# Revit family: ESTW
name_source: partatom
category: Mechanical Equipment
revit_build: Autodesk Revit 2018 (Build: 20170223_1515(x64)
units: mm (PartAtom-declared; Revit-internal decimal feet)

## family parameters
Always vertical = Yes
Cut with Voids When Loaded = No
Part Type = Normal
Room Calculation Point = No
Round Connector Dimension = Use Radius
Shared = No
Work Plane-Based = No

## types (192) — shared parameters
Description = Series Fan Powered Air Terminal with ECM Motor and Hot Water Coil
Discharge Flange = 1"
Discharge Height "Y" = 17 1/2"
Enclosure Depth = 6 1/2"
Enclosure Length = 22 1/4"
Enclosure Width = 11 1/8"
HWC Conn "B" = 3 3/8"
HWC Conn "C" = 1 39/64"
HWC Conn Top = 1 7/16"
HWConnec Length = 4"
Inlet S dim = 5 1/2"
Manufacturer = Anemostat
Model = ESTW
URL = http://www.anemostat.com

## per-type parameters (varying)
- ESTW 1/2-hp - 06L 1ROW COIL W/O S/ELBOW: Connector Bottom LH=Yes; Connector Bottom RH=No; Connector Top LH=Yes; Connector Top RH=No; Diameter=5 7/8"; Discharge Width "X"=20"; Duct Inlet Radius=3"; Elbow for LH=No; Elbow for RH=No; Enclosure for LH=Yes; Enclosure for RH=No; HWC Conn=0"; HWC Depth "Z"=12 1/4"; HWC for LH=Yes; HWC for RH=No; Height=18"; Induction Width "C"=17"; Induction for LH=Yes; Induction for RH=No; Inlet for LH=Yes; Inlet for RH=No; Length=40"; Q5A=18"; Q5B=20"; Q5Q=18"; Radius=2 15/16"; Width=40"
- ESTW 1-hp - 09L 1ROW COIL W/O S/ELBOW: Connector Bottom LH=Yes; Connector Bottom RH=No; Connector Top LH=Yes; Connector Top RH=No; Diameter=8 7/8"; Discharge Width "X"=24"; Duct Inlet Radius=4"; Elbow for LH=No; Elbow for RH=No; Enclosure for LH=Yes; Enclosure for RH=No; HWC Conn=0"; HWC Depth "Z"=12 1/4"; HWC for LH=Yes; HWC for RH=No; Height=20"; Induction Width "C"=21"; Induction for LH=Yes; Induction for RH=No; Inlet for LH=Yes; Inlet for RH=No; Length=48"; Q5A=20"; Q5B=24"; Q5Q=20"; Radius=4 7/16"; Width=48"
- ESTW 1/3-hp - 08L 1ROW COIL W/O S/ELBOW: Connector Bottom LH=Yes; Connector Bottom RH=No; Connector Top LH=Yes; Connector Top RH=No; Diameter=7 7/8"; Discharge Width "X"=20"; Duct Inlet Radius=4"; Elbow for LH=No; Elbow for RH=No; Enclosure for LH=Yes; Enclosure for RH=No; HWC Conn=1"; HWC Depth "Z"=12 1/4"; HWC for LH=Yes; HWC for RH=No; Height=18"; Induction Width "C"=12"; Induction for LH=Yes; Induction for RH=No; Inlet for LH=Yes; Inlet for RH=No; Length=36"; Q5A=18"; Q5B=18"; Q5Q=18"; Radius=3 15/16"; Width=32"
- ESTW 1/3-hp - 10L 1ROW COIL W/O S/ELBOW: Connector Bottom LH=Yes; Connector Bottom RH=No; Connector Top LH=Yes; Connector Top RH=No; Diameter=9 7/8"; Discharge Width "X"=20"; Duct Inlet Radius=5"; Elbow for LH=No; Elbow for RH=No; Enclosure for LH=Yes; Enclosure for RH=No; HWC Conn=0"; HWC Depth "Z"=12 1/4"; HWC for LH=Yes; HWC for RH=No; Height=18"; Induction Width "C"=12"; Induction for LH=Yes; Induction for RH=No; Inlet for LH=Yes; Inlet for RH=No; Length=36"; Q5A=18"; Q5B=18"; Q5Q=18"; Radius=4 15/16"; Width=32"
- ESTW 1/2-hp - 07L 1ROW COIL W/O S/ELBOW: Connector Bottom LH=Yes; Connector Bottom RH=No; Connector Top LH=Yes; Connector Top RH=No; Diameter=6 7/8"; Discharge Width "X"=20"; Duct Inlet Radius=3"; Elbow for LH=No; Elbow for RH=No; Enclosure for LH=Yes; Enclosure for RH=No; HWC Conn=0"; HWC Depth "Z"=12 1/4"; HWC for LH=Yes; HWC for RH=No; Height=18"; Induction Width "C"=17"; Induction for LH=Yes; Induction for RH=No; Inlet for LH=Yes; Inlet for RH=No; Length=40"; Q5A=18"; Q5B=20"; Q5Q=18"; Radius=3 7/16"; Width=40"
- ESTW 1/2-hp - 08L 1ROW COIL W/O S/ELBOW: Connector Bottom LH=Yes; Connector Bottom RH=No; Connector Top LH=Yes; Connector Top RH=No; Diameter=7 7/8"; Discharge Width "X"=20"; Duct Inlet Radius=4"; Elbow for LH=No; Elbow for RH=No; Enclosure for LH=Yes; Enclosure for RH=No; HWC Conn=0"; HWC Depth "Z"=12 1/4"; HWC for LH=Yes; HWC for RH=No; Height=18"; Induction Width "C"=17"; Induction for LH=Yes; Induction for RH=No; Inlet for LH=Yes; Inlet for RH=No; Length=40"; Q5A=18"; Q5B=20"; Q5Q=18"; Radius=3 15/16"; Width=40"
- ESTW 1/2-hp - 08L 2ROW COIL W/O S/ELBOW: Connector Bottom LH=Yes; Connector Bottom RH=No; Connector Top LH=Yes; Connector Top RH=No; Diameter=7 7/8"; Discharge Width "X"=20"; Duct Inlet Radius=4"; Elbow for LH=No; Elbow for RH=No; Enclosure for LH=Yes; Enclosure for RH=No; HWC Conn=0"; HWC Depth "Z"=13 1/2"; HWC for LH=Yes; HWC for RH=No; Height=18"; Induction Width "C"=17"; Induction for LH=Yes; Induction for RH=No; Inlet for LH=Yes; Inlet for RH=No; Length=40"; Q5A=18"; Q5B=20"; Q5Q=18"; Radius=3 15/16"; Width=40"
- ESTW 1/2-hp - 06L 2ROW COIL W/O S/ELBOW: Connector Bottom LH=Yes; Connector Bottom RH=No; Connector Top LH=Yes; Connector Top RH=No; Diameter=5 7/8"; Discharge Width "X"=20"; Duct Inlet Radius=3"; Elbow for LH=No; Elbow for RH=No; Enclosure for LH=Yes; Enclosure for RH=No; HWC Conn=0"; HWC Depth "Z"=13 1/2"; HWC for LH=Yes; HWC for RH=No; Height=18"; Induction Width "C"=17"; Induction for LH=Yes; Induction for RH=No; Inlet for LH=Yes; Inlet for RH=No; Length=40"; Q5A=18"; Q5B=20"; Q5Q=18"; Radius=2 15/16"; Width=40"
- ESTW 1/3-hp - 08L 2ROW COIL W/O S/ELBOW: Connector Bottom LH=Yes; Connector Bottom RH=No; Connector Top LH=Yes; Connector Top RH=No; Diameter=7 7/8"; Discharge Width "X"=20"; Duct Inlet Radius=4"; Elbow for LH=No; Elbow for RH=No; Enclosure for LH=Yes; Enclosure for RH=No; HWC Conn=1"; HWC Depth "Z"=13 1/2"; HWC for LH=Yes; HWC for RH=No; Height=18"; Induction Width "C"=12"; Induction for LH=Yes; Induction for RH=No; Inlet for LH=Yes; Inlet for RH=No; Length=36"; Q5A=18"; Q5B=18"; Q5Q=18"; Radius=3 15/16"; Width=32"
- ESTW 1/3-hp - 09L 2ROW COIL W/O S/ELBOW: Connector Bottom LH=Yes; Connector Bottom RH=No; Connector Top LH=Yes; Connector Top RH=No; Diameter=8 7/8"; Discharge Width "X"=20"; Duct Inlet Radius=4"; Elbow for LH=No; Elbow for RH=No; Enclosure for LH=Yes; Enclosure for RH=No; HWC Conn=0"; HWC Depth "Z"=13 1/2"; HWC for LH=Yes; HWC for RH=No; Height=18"; Induction Width "C"=12"; Induction for LH=Yes; Induction for RH=No; Inlet for LH=Yes; Inlet for RH=No; Length=36"; Q5A=18"; Q5B=18"; Q5Q=18"; Radius=4 7/16"; Width=32"
- ESTW 1/3-hp - 10L 2ROW COIL W/O S/ELBOW: Connector Bottom LH=Yes; Connector Bottom RH=No; Connector Top LH=Yes; Connector Top RH=No; Diameter=9 7/8"; Discharge Width "X"=20"; Duct Inlet Radius=5"; Elbow for LH=No; Elbow for RH=No; Enclosure for LH=Yes; Enclosure for RH=No; HWC Conn=0"; HWC Depth "Z"=13 1/2"; HWC for LH=Yes; HWC for RH=No; Height=18"; Induction Width "C"=12"; Induction for LH=Yes; Induction for RH=No; Inlet for LH=Yes; Inlet for RH=No; Length=36"; Q5A=18"; Q5B=18"; Q5Q=18"; Radius=4 15/16"; Width=32"
- ESTW 1-hp - 16L 2ROW COIL W/O S/ELBOW: Connector Bottom LH=Yes; Connector Bottom RH=No; Connector Top LH=Yes; Connector Top RH=No; Diameter=15 7/8"; Discharge Width "X"=24"; Duct Inlet Radius=8"; Elbow for LH=No; Elbow for RH=No; Enclosure for LH=Yes; Enclosure for RH=No; HWC Conn=0"; HWC Depth "Z"=13 1/2"; HWC for LH=Yes; HWC for RH=No; Height=20"; Induction Width "C"=21"; Induction for LH=Yes; Induction for RH=No; Inlet for LH=Yes; Inlet for RH=No; Length=48"; Q5A=20"; Q5B=24"; Q5Q=20"; Radius=7 15/16"; Width=48"
- ESTW 1/2-hp - 06R 1ROW COIL W/O S/ELBOW: Connector Bottom LH=No; Connector Bottom RH=Yes; Connector Top LH=No; Connector Top RH=Yes; Diameter=5 7/8"; Discharge Width "X"=20"; Duct Inlet Radius=3"; Elbow for LH=No; Elbow for RH=No; Enclosure for LH=No; Enclosure for RH=Yes; HWC Conn=0"; HWC Depth "Z"=12 1/4"; HWC for LH=No; HWC for RH=Yes; Height=18"; Induction Width "C"=17"; Induction for LH=No; Induction for RH=Yes; Inlet for LH=No; Inlet for RH=Yes; Length=40"; Q5A=18"; Q5B=20"; Q5Q=18"; Radius=2 15/16"; Width=40"
- ESTW 1/2-hp - 06R 2ROW COIL W/O S/ELBOW: Connector Bottom LH=No; Connector Bottom RH=Yes; Connector Top LH=No; Connector Top RH=Yes; Diameter=5 7/8"; Discharge Width "X"=20"; Duct Inlet Radius=3"; Elbow for LH=No; Elbow for RH=No; Enclosure for LH=No; Enclosure for RH=Yes; HWC Conn=0"; HWC Depth "Z"=13 1/2"; HWC for LH=No; HWC for RH=Yes; Height=18"; Induction Width "C"=17"; Induction for LH=No; Induction for RH=Yes; Inlet for LH=No; Inlet for RH=Yes; Length=40"; Q5A=18"; Q5B=20"; Q5Q=18"; Radius=2 15/16"; Width=40"
- ESTW 1/2-hp - 07R 1ROW COIL W/O S/ELBOW: Connector Bottom LH=No; Connector Bottom RH=Yes; Connector Top LH=No; Connector Top RH=Yes; Diameter=6 7/8"; Discharge Width "X"=20"; Duct Inlet Radius=3"; Elbow for LH=No; Elbow for RH=No; Enclosure for LH=No; Enclosure for RH=Yes; HWC Conn=0"; HWC Depth "Z"=12 1/4"; HWC for LH=No; HWC for RH=Yes; Height=18"; Induction Width "C"=17"; Induction for LH=No; Induction for RH=Yes; Inlet for LH=No; Inlet for RH=Yes; Length=40"; Q5A=18"; Q5B=20"; Q5Q=18"; Radius=3 7/16"; Width=40"
- ESTW 1/2-hp - 08R 1ROW COIL W/O S/ELBOW: Connector Bottom LH=No; Connector Bottom RH=Yes; Connector Top LH=No; Connector Top RH=Yes; Diameter=7 7/8"; Discharge Width "X"=20"; Duct Inlet Radius=4"; Elbow for LH=No; Elbow for RH=No; Enclosure for LH=No; Enclosure for RH=Yes; HWC Conn=0"; HWC Depth "Z"=12 1/4"; HWC for LH=No; HWC for RH=Yes; Height=18"; Induction Width "C"=17"; Induction for LH=No; Induction for RH=Yes; Inlet for LH=No; Inlet for RH=Yes; Length=40"; Q5A=18"; Q5B=20"; Q5Q=18"; Radius=3 15/16"; Width=40"
- ESTW 1/2-hp - 08R 2ROW COIL W/O S/ELBOW: Connector Bottom LH=No; Connector Bottom RH=Yes; Connector Top LH=No; Connector Top RH=Yes; Diameter=7 7/8"; Discharge Width "X"=20"; Duct Inlet Radius=4"; Elbow for LH=No; Elbow for RH=No; Enclosure for LH=No; Enclosure for RH=Yes; HWC Conn=0"; HWC Depth "Z"=13 1/2"; HWC for LH=No; HWC for RH=Yes; Height=18"; Induction Width "C"=17"; Induction for LH=No; Induction for RH=Yes; Inlet for LH=No; Inlet for RH=Yes; Length=40"; Q5A=18"; Q5B=20"; Q5Q=18"; Radius=3 15/16"; Width=40"
- ESTW 1/3-hp - 08R 1ROW COIL W/O S/ELBOW: Connector Bottom LH=No; Connector Bottom RH=No; Connector Top LH=No; Connector Top RH=Yes; Diameter=7 7/8"; Discharge Width "X"=20"; Duct Inlet Radius=4"; Elbow for LH=No; Elbow for RH=No; Enclosure for LH=No; Enclosure for RH=Yes; HWC Conn=1"; HWC Depth "Z"=12 1/4"; HWC for LH=No; HWC for RH=Yes; Height=18"; Induction Width "C"=12"; Induction for LH=No; Induction for RH=Yes; Inlet for LH=No; Inlet for RH=Yes; Length=36"; Q5A=18"; Q5B=18"; Q5Q=18"; Radius=3 15/16"; Width=32"
- ESTW 1/3-hp - 09R 2ROW COIL W/O S/ELBOW: Connector Bottom LH=No; Connector Bottom RH=Yes; Connector Top LH=No; Connector Top RH=Yes; Diameter=8 7/8"; Discharge Width "X"=20"; Duct Inlet Radius=4"; Elbow for LH=No; Elbow for RH=No; Enclosure for LH=No; Enclosure for RH=Yes; HWC Conn=0"; HWC Depth "Z"=13 1/2"; HWC for LH=No; HWC for RH=Yes; Height=18"; Induction Width "C"=12"; Induction for LH=No; Induction for RH=Yes; Inlet for LH=No; Inlet for RH=Yes; Length=36"; Q5A=18"; Q5B=18"; Q5Q=18"; Radius=4 7/16"; Width=32"
- ESTW 1/3-hp - 10R 1ROW COIL W/O S/ELBOW: Connector Bottom LH=No; Connector Bottom RH=Yes; Connector Top LH=No; Connector Top RH=Yes; Diameter=9 7/8"; Discharge Width "X"=20"; Duct Inlet Radius=5"; Elbow for LH=No; Elbow for RH=No; Enclosure for LH=No; Enclosure for RH=Yes; HWC Conn=0"; HWC Depth "Z"=12 1/4"; HWC for LH=No; HWC for RH=Yes; Height=18"; Induction Width "C"=12"; Induction for LH=No; Induction for RH=Yes; Inlet for LH=No; Inlet for RH=Yes; Length=36"; Q5A=18"; Q5B=18"; Q5Q=18"; Radius=4 15/16"; Width=32"
- ESTW 1-hp - 09R 1ROW COIL W/O S/ELBOW: Connector Bottom LH=No; Connector Bottom RH=Yes; Connector Top LH=No; Connector Top RH=Yes; Diameter=8 7/8"; Discharge Width "X"=24"; Duct Inlet Radius=4"; Elbow for LH=No; Elbow for RH=No; Enclosure for LH=No; Enclosure for RH=Yes; HWC Conn=0"; HWC Depth "Z"=12 1/4"; HWC for LH=No; HWC for RH=Yes; Height=20"; Induction Width "C"=21"; Induction for LH=No; Induction for RH=Yes; Inlet for LH=No; Inlet for RH=Yes; Length=48"; Q5A=20"; Q5B=24"; Q5Q=20"; Radius=4 7/16"; Width=48"
- ESTW 1-hp - 16R 2ROW COIL W/O S/ELBOW: Connector Bottom LH=No; Connector Bottom RH=Yes; Connector Top LH=No; Connector Top RH=Yes; Diameter=15 7/8"; Discharge Width "X"=24"; Duct Inlet Radius=8"; Elbow for LH=No; Elbow for RH=No; Enclosure for LH=No; Enclosure for RH=Yes; HWC Conn=0"; HWC Depth "Z"=13 1/2"; HWC for LH=No; HWC for RH=Yes; Height=20"; Induction Width "C"=21"; Induction for LH=No; Induction for RH=Yes; Inlet for LH=No; Inlet for RH=Yes; Length=48"; Q5A=20"; Q5B=24"; Q5Q=20"; Radius=7 15/16"; Width=48"
- ESTW 1/2-hp - 06L 1ROW COIL WITH S/ELBOW: Connector Bottom LH=Yes; Connector Bottom RH=No; Connector Top LH=Yes; Connector Top RH=No; Diameter=5 7/8"; Discharge Width "X"=20"; Duct Inlet Radius=3"; Elbow for LH=Yes; Elbow for RH=No; Enclosure for LH=Yes; Enclosure for RH=No; HWC Conn=0"; HWC Depth "Z"=12 1/4"; HWC for LH=Yes; HWC for RH=No; Height=18"; Induction Width "C"=17"; Induction for LH=Yes; Induction for RH=No; Inlet for LH=Yes; Inlet for RH=No; Length=40"; Q5A=18"; Q5B=20"; Q5Q=18"; Radius=2 15/16"; Width=40"
- ESTW 1/2-hp - 06R 1ROW COIL WITH S/ELBOW: Connector Bottom LH=No; Connector Bottom RH=Yes; Connector Top LH=No; Connector Top RH=Yes; Diameter=5 7/8"; Discharge Width "X"=20"; Duct Inlet Radius=3"; Elbow for LH=No; Elbow for RH=Yes; Enclosure for LH=No; Enclosure for RH=Yes; HWC Conn=0"; HWC Depth "Z"=12 1/4"; HWC for LH=No; HWC for RH=Yes; Height=18"; Induction Width "C"=17"; Induction for LH=No; Induction for RH=Yes; Inlet for LH=No; Inlet for RH=Yes; Length=40"; Q5A=18"; Q5B=20"; Q5Q=18"; Radius=2 15/16"; Width=40"
- ESTW 1/2-hp - 06L 2ROW COIL WITH S/ELBOW: Connector Bottom LH=Yes; Connector Bottom RH=No; Connector Top LH=Yes; Connector Top RH=No; Diameter=5 7/8"; Discharge Width "X"=20"; Duct Inlet Radius=3"; Elbow for LH=Yes; Elbow for RH=No; Enclosure for LH=Yes; Enclosure for RH=No; HWC Conn=0"; HWC Depth "Z"=13 1/2"; HWC for LH=Yes; HWC for RH=No; Height=18"; Induction Width "C"=17"; Induction for LH=Yes; Induction for RH=No; Inlet for LH=Yes; Inlet for RH=No; Length=40"; Q5A=18"; Q5B=20"; Q5Q=18"; Radius=2 15/16"; Width=40"
- ESTW 1/2-hp - 06R 2ROW COIL WITH S/ELBOW: Connector Bottom LH=No; Connector Bottom RH=Yes; Connector Top LH=No; Connector Top RH=Yes; Diameter=5 7/8"; Discharge Width "X"=20"; Duct Inlet Radius=3"; Elbow for LH=No; Elbow for RH=Yes; Enclosure for LH=No; Enclosure for RH=Yes; HWC Conn=0"; HWC Depth "Z"=13 1/2"; HWC for LH=No; HWC for RH=Yes; Height=18"; Induction Width "C"=17"; Induction for LH=No; Induction for RH=Yes; Inlet for LH=No; Inlet for RH=Yes; Length=40"; Q5A=18"; Q5B=20"; Q5Q=18"; Radius=2 15/16"; Width=40"
- ESTW 1/2-hp - 07L 1ROW COIL WITH S/ELBOW: Connector Bottom LH=Yes; Connector Bottom RH=No; Connector Top LH=Yes; Connector Top RH=No; Diameter=6 7/8"; Discharge Width "X"=20"; Duct Inlet Radius=3"; Elbow for LH=Yes; Elbow for RH=No; Enclosure for LH=Yes; Enclosure for RH=No; HWC Conn=0"; HWC Depth "Z"=12 1/4"; HWC for LH=Yes; HWC for RH=No; Height=18"; Induction Width "C"=17"; Induction for LH=Yes; Induction for RH=No; Inlet for LH=Yes; Inlet for RH=No; Length=40"; Q5A=18"; Q5B=20"; Q5Q=18"; Radius=3 7/16"; Width=40"
- ESTW 1/2-hp - 07R 1ROW COIL WITH S/ELBOW: Connector Bottom LH=No; Connector Bottom RH=Yes; Connector Top LH=No; Connector Top RH=Yes; Diameter=6 7/8"; Discharge Width "X"=20"; Duct Inlet Radius=3"; Elbow for LH=No; Elbow for RH=Yes; Enclosure for LH=No; Enclosure for RH=Yes; HWC Conn=0"; HWC Depth "Z"=12 1/4"; HWC for LH=No; HWC for RH=Yes; Height=18"; Induction Width "C"=17"; Induction for LH=No; Induction for RH=Yes; Inlet for LH=No; Inlet for RH=Yes; Length=40"; Q5A=18"; Q5B=20"; Q5Q=18"; Radius=3 7/16"; Width=40"
- ESTW 1/2-hp - 07L 2ROW COIL W/O S/ELBOW: Connector Bottom LH=Yes; Connector Bottom RH=No; Connector Top LH=Yes; Connector Top RH=No; Diameter=6 7/8"; Discharge Width "X"=20"; Duct Inlet Radius=3"; Elbow for LH=No; Elbow for RH=No; Enclosure for LH=Yes; Enclosure for RH=No; HWC Conn=0"; HWC Depth "Z"=13 1/2"; HWC for LH=Yes; HWC for RH=No; Height=18"; Induction Width "C"=17"; Induction for LH=Yes; Induction for RH=No; Inlet for LH=Yes; Inlet for RH=No; Length=40"; Q5A=18"; Q5B=20"; Q5Q=18"; Radius=3 7/16"; Width=40"
- ESTW 1/2-hp - 07L 2ROW COIL WITH S/ELBOW: Connector Bottom LH=Yes; Connector Bottom RH=No; Connector Top LH=Yes; Connector Top RH=No; Diameter=6 7/8"; Discharge Width "X"=20"; Duct Inlet Radius=3"; Elbow for LH=Yes; Elbow for RH=No; Enclosure for LH=Yes; Enclosure for RH=No; HWC Conn=0"; HWC Depth "Z"=13 1/2"; HWC for LH=Yes; HWC for RH=No; Height=18"; Induction Width "C"=17"; Induction for LH=Yes; Induction for RH=No; Inlet for LH=Yes; Inlet for RH=No; Length=40"; Q5A=18"; Q5B=20"; Q5Q=18"; Radius=3 7/16"; Width=40"
- ESTW 1/2-hp - 07R 2ROW COIL WITH S/ELBOW: Connector Bottom LH=No; Connector Bottom RH=Yes; Connector Top LH=No; Connector Top RH=Yes; Diameter=6 7/8"; Discharge Width "X"=20"; Duct Inlet Radius=3"; Elbow for LH=No; Elbow for RH=Yes; Enclosure for LH=No; Enclosure for RH=Yes; HWC Conn=0"; HWC Depth "Z"=13 1/2"; HWC for LH=No; HWC for RH=Yes; Height=18"; Induction Width "C"=17"; Induction for LH=No; Induction for RH=Yes; Inlet for LH=No; Inlet for RH=Yes; Length=40"; Q5A=18"; Q5B=20"; Q5Q=18"; Radius=3 7/16"; Width=40"
- ESTW 1/2-hp - 07R 2ROW COIL W/O S/ELBOW: Connector Bottom LH=No; Connector Bottom RH=Yes; Connector Top LH=No; Connector Top RH=Yes; Diameter=6 7/8"; Discharge Width "X"=20"; Duct Inlet Radius=3"; Elbow for LH=No; Elbow for RH=No; Enclosure for LH=No; Enclosure for RH=Yes; HWC Conn=0"; HWC Depth "Z"=13 1/2"; HWC for LH=No; HWC for RH=Yes; Height=18"; Induction Width "C"=17"; Induction for LH=No; Induction for RH=Yes; Inlet for LH=No; Inlet for RH=Yes; Length=40"; Q5A=18"; Q5B=20"; Q5Q=18"; Radius=3 7/16"; Width=40"
- ESTW 1/2-hp - 08R 2ROW COIL WITH S/ELBOW: Connector Bottom LH=No; Connector Bottom RH=Yes; Connector Top LH=No; Connector Top RH=Yes; Diameter=7 7/8"; Discharge Width "X"=20"; Duct Inlet Radius=4"; Elbow for LH=No; Elbow for RH=Yes; Enclosure for LH=No; Enclosure for RH=Yes; HWC Conn=0"; HWC Depth "Z"=13 1/2"; HWC for LH=No; HWC for RH=Yes; Height=18"; Induction Width "C"=17"; Induction for LH=No; Induction for RH=Yes; Inlet for LH=No; Inlet for RH=Yes; Length=40"; Q5A=18"; Q5B=20"; Q5Q=18"; Radius=3 15/16"; Width=40"
- ESTW 1/2-hp - 08L 1ROW COIL WITH S/ELBOW: Connector Bottom LH=Yes; Connector Bottom RH=No; Connector Top LH=Yes; Connector Top RH=No; Diameter=7 7/8"; Discharge Width "X"=20"; Duct Inlet Radius=4"; Elbow for LH=Yes; Elbow for RH=No; Enclosure for LH=Yes; Enclosure for RH=No; HWC Conn=0"; HWC Depth "Z"=12 1/4"; HWC for LH=Yes; HWC for RH=No; Height=18"; Induction Width "C"=17"; Induction for LH=Yes; Induction for RH=No; Inlet for LH=Yes; Inlet for RH=No; Length=40"; Q5A=18"; Q5B=20"; Q5Q=18"; Radius=3 15/16"; Width=40"
- ESTW 1/2-hp - 08L 2ROW COIL WITH S/ELBOW: Connector Bottom LH=Yes; Connector Bottom RH=No; Connector Top LH=Yes; Connector Top RH=No; Diameter=7 7/8"; Discharge Width "X"=20"; Duct Inlet Radius=4"; Elbow for LH=Yes; Elbow for RH=No; Enclosure for LH=Yes; Enclosure for RH=No; HWC Conn=0"; HWC Depth "Z"=13 1/2"; HWC for LH=Yes; HWC for RH=No; Height=18"; Induction Width "C"=17"; Induction for LH=Yes; Induction for RH=No; Inlet for LH=Yes; Inlet for RH=No; Length=40"; Q5A=18"; Q5B=20"; Q5Q=18"; Radius=3 15/16"; Width=40"
- ESTW 1/2-hp - 08R 1ROW COIL WITH S/ELBOW: Connector Bottom LH=No; Connector Bottom RH=Yes; Connector Top LH=No; Connector Top RH=Yes; Diameter=7 7/8"; Discharge Width "X"=20"; Duct Inlet Radius=4"; Elbow for LH=No; Elbow for RH=Yes; Enclosure for LH=No; Enclosure for RH=Yes; HWC Conn=0"; HWC Depth "Z"=12 1/4"; HWC for LH=No; HWC for RH=Yes; Height=18"; Induction Width "C"=17"; Induction for LH=No; Induction for RH=Yes; Inlet for LH=No; Inlet for RH=Yes; Length=40"; Q5A=18"; Q5B=20"; Q5Q=18"; Radius=3 15/16"; Width=40"
- ESTW 1/3-hp - 08L 1ROW COIL WITH S/ELBOW: Connector Bottom LH=Yes; Connector Bottom RH=No; Connector Top LH=Yes; Connector Top RH=No; Diameter=7 7/8"; Discharge Width "X"=20"; Duct Inlet Radius=4"; Elbow for LH=Yes; Elbow for RH=No; Enclosure for LH=Yes; Enclosure for RH=No; HWC Conn=1"; HWC Depth "Z"=12 1/4"; HWC for LH=Yes; HWC for RH=No; Height=18"; Induction Width "C"=12"; Induction for LH=Yes; Induction for RH=No; Inlet for LH=Yes; Inlet for RH=No; Length=36"; Q5A=18"; Q5B=18"; Q5Q=18"; Radius=3 15/16"; Width=32"
- ESTW 1/3-hp - 08L 2ROW COIL WITH S/ELBOW: Connector Bottom LH=Yes; Connector Bottom RH=No; Connector Top LH=Yes; Connector Top RH=No; Diameter=7 7/8"; Discharge Width "X"=20"; Duct Inlet Radius=4"; Elbow for LH=Yes; Elbow for RH=No; Enclosure for LH=Yes; Enclosure for RH=No; HWC Conn=1"; HWC Depth "Z"=13 1/2"; HWC for LH=Yes; HWC for RH=No; Height=18"; Induction Width "C"=12"; Induction for LH=Yes; Induction for RH=No; Inlet for LH=Yes; Inlet for RH=No; Length=36"; Q5A=18"; Q5B=18"; Q5Q=18"; Radius=3 15/16"; Width=32"
- ESTW 1/3-hp - 08R 1ROW COIL WITH S/ELBOW: Connector Bottom LH=No; Connector Bottom RH=Yes; Connector Top LH=No; Connector Top RH=Yes; Diameter=7 7/8"; Discharge Width "X"=20"; Duct Inlet Radius=4"; Elbow for LH=No; Elbow for RH=Yes; Enclosure for LH=No; Enclosure for RH=Yes; HWC Conn=1"; HWC Depth "Z"=12 1/4"; HWC for LH=No; HWC for RH=Yes; Height=18"; Induction Width "C"=12"; Induction for LH=No; Induction for RH=Yes; Inlet for LH=No; Inlet for RH=Yes; Length=36"; Q5A=18"; Q5B=18"; Q5Q=18"; Radius=3 15/16"; Width=32"
- ESTW 1/3-hp - 08R 2ROW COIL W/O S/ELBOW: Connector Bottom LH=No; Connector Bottom RH=Yes; Connector Top LH=No; Connector Top RH=Yes; Diameter=7 7/8"; Discharge Width "X"=20"; Duct Inlet Radius=4"; Elbow for LH=No; Elbow for RH=No; Enclosure for LH=No; Enclosure for RH=Yes; HWC Conn=1"; HWC Depth "Z"=13 1/2"; HWC for LH=No; HWC for RH=Yes; Height=18"; Induction Width "C"=12"; Induction for LH=No; Induction for RH=Yes; Inlet for LH=No; Inlet for RH=Yes; Length=36"; Q5A=18"; Q5B=18"; Q5Q=18"; Radius=3 15/16"; Width=32"
- ESTW 1/3-hp - 08R 2ROW COIL WITH S/ELBOW: Connector Bottom LH=No; Connector Bottom RH=Yes; Connector Top LH=No; Connector Top RH=Yes; Diameter=7 7/8"; Discharge Width "X"=20"; Duct Inlet Radius=4"; Elbow for LH=No; Elbow for RH=Yes; Enclosure for LH=No; Enclosure for RH=Yes; HWC Conn=1"; HWC Depth "Z"=13 1/2"; HWC for LH=No; HWC for RH=Yes; Height=18"; Induction Width "C"=12"; Induction for LH=No; Induction for RH=Yes; Inlet for LH=No; Inlet for RH=Yes; Length=36"; Q5A=18"; Q5B=18"; Q5Q=18"; Radius=3 15/16"; Width=32"
- ESTW 1/3-hp - 09L 2ROW COIL WITH S/ELBOW: Connector Bottom LH=Yes; Connector Bottom RH=No; Connector Top LH=Yes; Connector Top RH=No; Diameter=8 7/8"; Discharge Width "X"=20"; Duct Inlet Radius=4"; Elbow for LH=Yes; Elbow for RH=No; Enclosure for LH=Yes; Enclosure for RH=No; HWC Conn=0"; HWC Depth "Z"=13 1/2"; HWC for LH=Yes; HWC for RH=No; Height=18"; Induction Width "C"=12"; Induction for LH=Yes; Induction for RH=No; Inlet for LH=Yes; Inlet for RH=No; Length=36"; Q5A=18"; Q5B=18"; Q5Q=18"; Radius=4 7/16"; Width=32"
- ESTW 1/3-hp - 09R 2ROW COIL WITH S/ELBOW: Connector Bottom LH=No; Connector Bottom RH=Yes; Connector Top LH=No; Connector Top RH=Yes; Diameter=8 7/8"; Discharge Width "X"=20"; Duct Inlet Radius=4"; Elbow for LH=No; Elbow for RH=No; Enclosure for LH=No; Enclosure for RH=Yes; HWC Conn=0"; HWC Depth "Z"=13 1/2"; HWC for LH=No; HWC for RH=Yes; Height=18"; Induction Width "C"=12"; Induction for LH=No; Induction for RH=Yes; Inlet for LH=No; Inlet for RH=Yes; Length=36"; Q5A=18"; Q5B=18"; Q5Q=18"; Radius=4 7/16"; Width=32"
- ESTW 1/3-hp - 09L 1ROW COIL W/O S/ELBOW: Connector Bottom LH=Yes; Connector Bottom RH=No; Connector Top LH=Yes; Connector Top RH=No; Diameter=8 7/8"; Discharge Width "X"=20"; Duct Inlet Radius=4"; Elbow for LH=No; Elbow for RH=No; Enclosure for LH=Yes; Enclosure for RH=No; HWC Conn=0"; HWC Depth "Z"=12 1/4"; HWC for LH=Yes; HWC for RH=No; Height=18"; Induction Width "C"=12"; Induction for LH=Yes; Induction for RH=No; Inlet for LH=Yes; Inlet for RH=No; Length=36"; Q5A=18"; Q5B=18"; Q5Q=18"; Radius=4 7/16"; Width=32"
- ESTW 1/3-hp - 09L 1ROW COIL WITH S/ELBOW: Connector Bottom LH=Yes; Connector Bottom RH=No; Connector Top LH=Yes; Connector Top RH=No; Diameter=8 7/8"; Discharge Width "X"=20"; Duct Inlet Radius=4"; Elbow for LH=Yes; Elbow for RH=No; Enclosure for LH=Yes; Enclosure for RH=No; HWC Conn=0"; HWC Depth "Z"=12 1/4"; HWC for LH=Yes; HWC for RH=No; Height=18"; Induction Width "C"=12"; Induction for LH=Yes; Induction for RH=No; Inlet for LH=Yes; Inlet for RH=No; Length=36"; Q5A=18"; Q5B=18"; Q5Q=18"; Radius=4 7/16"; Width=32"
- ESTW 1/3-hp - 09R 1ROW COIL W/O S/ELBOW: Connector Bottom LH=No; Connector Bottom RH=Yes; Connector Top LH=No; Connector Top RH=Yes; Diameter=8 7/8"; Discharge Width "X"=20"; Duct Inlet Radius=4"; Elbow for LH=No; Elbow for RH=No; Enclosure for LH=No; Enclosure for RH=Yes; HWC Conn=0"; HWC Depth "Z"=12 1/4"; HWC for LH=No; HWC for RH=Yes; Height=18"; Induction Width "C"=12"; Induction for LH=No; Induction for RH=Yes; Inlet for LH=No; Inlet for RH=Yes; Length=36"; Q5A=18"; Q5B=18"; Q5Q=18"; Radius=4 7/16"; Width=32"
- ESTW 1/3-hp - 09R 1ROW COIL WITH S/ELBOW: Connector Bottom LH=No; Connector Bottom RH=Yes; Connector Top LH=No; Connector Top RH=Yes; Diameter=8 7/8"; Discharge Width "X"=20"; Duct Inlet Radius=4"; Elbow for LH=No; Elbow for RH=Yes; Enclosure for LH=No; Enclosure for RH=Yes; HWC Conn=0"; HWC Depth "Z"=12 1/4"; HWC for LH=No; HWC for RH=Yes; Height=18"; Induction Width "C"=12"; Induction for LH=No; Induction for RH=Yes; Inlet for LH=No; Inlet for RH=Yes; Length=36"; Q5A=18"; Q5B=18"; Q5Q=18"; Radius=4 7/16"; Width=32"
- ESTW 1/3-hp - 10L 1ROW COIL WITH S/ELBOW: Connector Bottom LH=Yes; Connector Bottom RH=No; Connector Top LH=Yes; Connector Top RH=No; Diameter=9 7/8"; Discharge Width "X"=20"; Duct Inlet Radius=5"; Elbow for LH=Yes; Elbow for RH=No; Enclosure for LH=Yes; Enclosure for RH=No; HWC Conn=0"; HWC Depth "Z"=12 1/4"; HWC for LH=Yes; HWC for RH=No; Height=18"; Induction Width "C"=12"; Induction for LH=Yes; Induction for RH=No; Inlet for LH=Yes; Inlet for RH=No; Length=36"; Q5A=18"; Q5B=18"; Q5Q=18"; Radius=4 15/16"; Width=32"
- ESTW 1/3-hp - 10R 1ROW COIL WITH S/ELBOW: Connector Bottom LH=No; Connector Bottom RH=Yes; Connector Top LH=No; Connector Top RH=Yes; Diameter=9 7/8"; Discharge Width "X"=20"; Duct Inlet Radius=5"; Elbow for LH=No; Elbow for RH=Yes; Enclosure for LH=No; Enclosure for RH=Yes; HWC Conn=0"; HWC Depth "Z"=12 1/4"; HWC for LH=No; HWC for RH=Yes; Height=18"; Induction Width "C"=12"; Induction for LH=No; Induction for RH=Yes; Inlet for LH=No; Inlet for RH=Yes; Length=36"; Q5A=18"; Q5B=18"; Q5Q=18"; Radius=4 15/16"; Width=32"
- ESTW 1/3-hp - 10L 2ROW COIL WITH S/ELBOW: Connector Bottom LH=Yes; Connector Bottom RH=No; Connector Top LH=Yes; Connector Top RH=No; Diameter=9 7/8"; Discharge Width "X"=20"; Duct Inlet Radius=5"; Elbow for LH=Yes; Elbow for RH=No; Enclosure for LH=Yes; Enclosure for RH=No; HWC Conn=0"; HWC Depth "Z"=13 1/2"; HWC for LH=Yes; HWC for RH=No; Height=18"; Induction Width "C"=12"; Induction for LH=Yes; Induction for RH=No; Inlet for LH=Yes; Inlet for RH=No; Length=36"; Q5A=18"; Q5B=18"; Q5Q=18"; Radius=4 15/16"; Width=32"
- ESTW 1/3-hp - 10R 2ROW COIL W/O S/ELBOW: Connector Bottom LH=No; Connector Bottom RH=Yes; Connector Top LH=No; Connector Top RH=Yes; Diameter=9 7/8"; Discharge Width "X"=20"; Duct Inlet Radius=5"; Elbow for LH=No; Elbow for RH=No; Enclosure for LH=No; Enclosure for RH=Yes; HWC Conn=0"; HWC Depth "Z"=13 1/2"; HWC for LH=No; HWC for RH=Yes; Height=18"; Induction Width "C"=12"; Induction for LH=No; Induction for RH=Yes; Inlet for LH=No; Inlet for RH=Yes; Length=36"; Q5A=18"; Q5B=18"; Q5Q=18"; Radius=4 15/16"; Width=32"
- ESTW 1/3-hp - 10R 2ROW COIL WITH S/ELBOW: Connector Bottom LH=No; Connector Bottom RH=Yes; Connector Top LH=No; Connector Top RH=Yes; Diameter=9 7/8"; Discharge Width "X"=20"; Duct Inlet Radius=5"; Elbow for LH=No; Elbow for RH=Yes; Enclosure for LH=No; Enclosure for RH=Yes; HWC Conn=0"; HWC Depth "Z"=13 1/2"; HWC for LH=No; HWC for RH=Yes; Height=18"; Induction Width "C"=12"; Induction for LH=No; Induction for RH=Yes; Inlet for LH=No; Inlet for RH=Yes; Length=36"; Q5A=18"; Q5B=18"; Q5Q=18"; Radius=4 15/16"; Width=32"
- ESTW 1/2-hp - 09L 1ROW COIL W/O S/ELBOW: Connector Bottom LH=Yes; Connector Bottom RH=No; Connector Top LH=Yes; Connector Top RH=No; Diameter=8 7/8"; Discharge Width "X"=20"; Duct Inlet Radius=4"; Elbow for LH=No; Elbow for RH=No; Enclosure for LH=Yes; Enclosure for RH=No; HWC Conn=0"; HWC Depth "Z"=12 1/4"; HWC for LH=Yes; HWC for RH=No; Height=18"; Induction Width "C"=17"; Induction for LH=Yes; Induction for RH=No; Inlet for LH=Yes; Inlet for RH=No; Length=40"; Q5A=18"; Q5B=20"; Q5Q=18"; Radius=4 7/16"; Width=40"
- ESTW 1/2-hp - 09R 1ROW COIL W/O S/ELBOW: Connector Bottom LH=No; Connector Bottom RH=Yes; Connector Top LH=No; Connector Top RH=Yes; Diameter=8 7/8"; Discharge Width "X"=20"; Duct Inlet Radius=4"; Elbow for LH=No; Elbow for RH=No; Enclosure for LH=No; Enclosure for RH=Yes; HWC Conn=0"; HWC Depth "Z"=12 1/4"; HWC for LH=No; HWC for RH=Yes; Height=18"; Induction Width "C"=17"; Induction for LH=No; Induction for RH=Yes; Inlet for LH=No; Inlet for RH=Yes; Length=40"; Q5A=18"; Q5B=20"; Q5Q=18"; Radius=4 7/16"; Width=40"
- ESTW 1/2-hp - 09L 1ROW COIL WITH S/ELBOW: Connector Bottom LH=Yes; Connector Bottom RH=No; Connector Top LH=Yes; Connector Top RH=No; Diameter=8 7/8"; Discharge Width "X"=20"; Duct Inlet Radius=4"; Elbow for LH=Yes; Elbow for RH=No; Enclosure for LH=Yes; Enclosure for RH=No; HWC Conn=0"; HWC Depth "Z"=12 1/4"; HWC for LH=Yes; HWC for RH=No; Height=18"; Induction Width "C"=17"; Induction for LH=Yes; Induction for RH=No; Inlet for LH=Yes; Inlet for RH=No; Length=40"; Q5A=18"; Q5B=20"; Q5Q=18"; Radius=4 7/16"; Width=40"
- ESTW 1/2-hp - 09R 1ROW COIL WITH S/ELBOW: Connector Bottom LH=No; Connector Bottom RH=Yes; Connector Top LH=No; Connector Top RH=Yes; Diameter=8 7/8"; Discharge Width "X"=20"; Duct Inlet Radius=4"; Elbow for LH=No; Elbow for RH=Yes; Enclosure for LH=No; Enclosure for RH=Yes; HWC Conn=0"; HWC Depth "Z"=12 1/4"; HWC for LH=No; HWC for RH=Yes; Height=18"; Induction Width "C"=17"; Induction for LH=No; Induction for RH=Yes; Inlet for LH=No; Inlet for RH=Yes; Length=40"; Q5A=18"; Q5B=20"; Q5Q=18"; Radius=4 7/16"; Width=40"
- ESTW 1/2-hp - 09L 2ROW COIL W/O S/ELBOW: Connector Bottom LH=Yes; Connector Bottom RH=No; Connector Top LH=Yes; Connector Top RH=No; Diameter=8 7/8"; Discharge Width "X"=20"; Duct Inlet Radius=4"; Elbow for LH=No; Elbow for RH=No; Enclosure for LH=Yes; Enclosure for RH=No; HWC Conn=0"; HWC Depth "Z"=13 1/2"; HWC for LH=Yes; HWC for RH=No; Height=18"; Induction Width "C"=17"; Induction for LH=Yes; Induction for RH=No; Inlet for LH=Yes; Inlet for RH=No; Length=40"; Q5A=18"; Q5B=20"; Q5Q=18"; Radius=4 7/16"; Width=40"
- ESTW 1/2-hp - 09R 2ROW COIL W/O S/ELBOW: Connector Bottom LH=No; Connector Bottom RH=Yes; Connector Top LH=No; Connector Top RH=Yes; Diameter=8 7/8"; Discharge Width "X"=20"; Duct Inlet Radius=4"; Elbow for LH=No; Elbow for RH=No; Enclosure for LH=No; Enclosure for RH=Yes; HWC Conn=0"; HWC Depth "Z"=13 1/2"; HWC for LH=No; HWC for RH=Yes; Height=18"; Induction Width "C"=17"; Induction for LH=No; Induction for RH=Yes; Inlet for LH=No; Inlet for RH=Yes; Length=40"; Q5A=18"; Q5B=20"; Q5Q=18"; Radius=4 7/16"; Width=40"
- ESTW 1/2-hp - 09L 2ROW COIL WITH S/ELBOW: Connector Bottom LH=Yes; Connector Bottom RH=No; Connector Top LH=Yes; Connector Top RH=No; Diameter=8 7/8"; Discharge Width "X"=20"; Duct Inlet Radius=4"; Elbow for LH=Yes; Elbow for RH=No; Enclosure for LH=Yes; Enclosure for RH=No; HWC Conn=0"; HWC Depth "Z"=13 1/2"; HWC for LH=Yes; HWC for RH=No; Height=18"; Induction Width "C"=17"; Induction for LH=Yes; Induction for RH=No; Inlet for LH=Yes; Inlet for RH=No; Length=40"; Q5A=18"; Q5B=20"; Q5Q=18"; Radius=4 7/16"; Width=40"
- ESTW 1/2-hp - 09R 2ROW COIL WITH S/ELBOW: Connector Bottom LH=No; Connector Bottom RH=Yes; Connector Top LH=No; Connector Top RH=Yes; Diameter=8 7/8"; Discharge Width "X"=20"; Duct Inlet Radius=4"; Elbow for LH=No; Elbow for RH=Yes; Enclosure for LH=No; Enclosure for RH=Yes; HWC Conn=0"; HWC Depth "Z"=13 1/2"; HWC for LH=No; HWC for RH=Yes; Height=18"; Induction Width "C"=17"; Induction for LH=No; Induction for RH=Yes; Inlet for LH=No; Inlet for RH=Yes; Length=40"; Q5A=18"; Q5B=20"; Q5Q=18"; Radius=4 7/16"; Width=40"
- ESTW 1/2-hp - 10L 1ROW COIL W/O S/ELBOW: Connector Bottom LH=Yes; Connector Bottom RH=No; Connector Top LH=Yes; Connector Top RH=No; Diameter=9 7/8"; Discharge Width "X"=20"; Duct Inlet Radius=5"; Elbow for LH=No; Elbow for RH=No; Enclosure for LH=Yes; Enclosure for RH=No; HWC Conn=0"; HWC Depth "Z"=12 1/4"; HWC for LH=Yes; HWC for RH=No; Height=18"; Induction Width "C"=17"; Induction for LH=Yes; Induction for RH=No; Inlet for LH=Yes; Inlet for RH=No; Length=40"; Q5A=18"; Q5B=20"; Q5Q=18"; Radius=4 15/16"; Width=40"
- ESTW 1/2-hp - 10R 1ROW COIL W/O S/ELBOW: Connector Bottom LH=No; Connector Bottom RH=Yes; Connector Top LH=No; Connector Top RH=Yes; Diameter=9 7/8"; Discharge Width "X"=20"; Duct Inlet Radius=5"; Elbow for LH=No; Elbow for RH=No; Enclosure for LH=No; Enclosure for RH=Yes; HWC Conn=0"; HWC Depth "Z"=12 1/4"; HWC for LH=No; HWC for RH=Yes; Height=18"; Induction Width "C"=17"; Induction for LH=No; Induction for RH=Yes; Inlet for LH=No; Inlet for RH=Yes; Length=40"; Q5A=18"; Q5B=20"; Q5Q=18"; Radius=4 15/16"; Width=40"
- ESTW 1/2-hp - 10R 1ROW COIL WITH S/ELBOW: Connector Bottom LH=No; Connector Bottom RH=Yes; Connector Top LH=No; Connector Top RH=Yes; Diameter=9 7/8"; Discharge Width "X"=20"; Duct Inlet Radius=5"; Elbow for LH=No; Elbow for RH=Yes; Enclosure for LH=No; Enclosure for RH=Yes; HWC Conn=0"; HWC Depth "Z"=12 1/4"; HWC for LH=No; HWC for RH=Yes; Height=18"; Induction Width "C"=17"; Induction for LH=No; Induction for RH=Yes; Inlet for LH=No; Inlet for RH=Yes; Length=40"; Q5A=18"; Q5B=20"; Q5Q=18"; Radius=4 15/16"; Width=40"
- ESTW 1/2-hp - 10L 1ROW COIL WITH S/ELBOW: Connector Bottom LH=Yes; Connector Bottom RH=No; Connector Top LH=Yes; Connector Top RH=No; Diameter=9 7/8"; Discharge Width "X"=20"; Duct Inlet Radius=5"; Elbow for LH=Yes; Elbow for RH=No; Enclosure for LH=Yes; Enclosure for RH=No; HWC Conn=0"; HWC Depth "Z"=12 1/4"; HWC for LH=Yes; HWC for RH=No; Height=18"; Induction Width "C"=17"; Induction for LH=Yes; Induction for RH=No; Inlet for LH=Yes; Inlet for RH=No; Length=40"; Q5A=18"; Q5B=20"; Q5Q=18"; Radius=4 15/16"; Width=40"
- ESTW 1/2-hp - 10L 2ROW COIL W/O S/ELBOW: Connector Bottom LH=Yes; Connector Bottom RH=No; Connector Top LH=Yes; Connector Top RH=No; Diameter=9 7/8"; Discharge Width "X"=20"; Duct Inlet Radius=5"; Elbow for LH=No; Elbow for RH=No; Enclosure for LH=Yes; Enclosure for RH=No; HWC Conn=0"; HWC Depth "Z"=13 1/2"; HWC for LH=Yes; HWC for RH=No; Height=18"; Induction Width "C"=17"; Induction for LH=Yes; Induction for RH=No; Inlet for LH=Yes; Inlet for RH=No; Length=40"; Q5A=18"; Q5B=20"; Q5Q=18"; Radius=4 15/16"; Width=40"
- ESTW 1/2-hp - 10R 2ROW COIL W/O S/ELBOW: Connector Bottom LH=No; Connector Bottom RH=Yes; Connector Top LH=No; Connector Top RH=Yes; Diameter=9 7/8"; Discharge Width "X"=20"; Duct Inlet Radius=5"; Elbow for LH=No; Elbow for RH=No; Enclosure for LH=No; Enclosure for RH=Yes; HWC Conn=0"; HWC Depth "Z"=13 1/2"; HWC for LH=No; HWC for RH=Yes; Height=18"; Induction Width "C"=17"; Induction for LH=No; Induction for RH=Yes; Inlet for LH=No; Inlet for RH=Yes; Length=40"; Q5A=18"; Q5B=20"; Q5Q=18"; Radius=4 15/16"; Width=40"
- ESTW 1/2-hp - 10R 2ROW COIL WITH S/ELBOW: Connector Bottom LH=No; Connector Bottom RH=Yes; Connector Top LH=No; Connector Top RH=Yes; Diameter=9 7/8"; Discharge Width "X"=20"; Duct Inlet Radius=5"; Elbow for LH=No; Elbow for RH=Yes; Enclosure for LH=No; Enclosure for RH=Yes; HWC Conn=0"; HWC Depth "Z"=13 1/2"; HWC for LH=No; HWC for RH=Yes; Height=18"; Induction Width "C"=17"; Induction for LH=No; Induction for RH=Yes; Inlet for LH=No; Inlet for RH=Yes; Length=40"; Q5A=18"; Q5B=20"; Q5Q=18"; Radius=4 15/16"; Width=40"
- ESTW 1/2-hp - 10L 2ROW COIL WITH S/ELBOW: Connector Bottom LH=Yes; Connector Bottom RH=No; Connector Top LH=Yes; Connector Top RH=No; Diameter=9 7/8"; Discharge Width "X"=20"; Duct Inlet Radius=5"; Elbow for LH=Yes; Elbow for RH=No; Enclosure for LH=Yes; Enclosure for RH=No; HWC Conn=0"; HWC Depth "Z"=13 1/2"; HWC for LH=Yes; HWC for RH=No; Height=18"; Induction Width "C"=17"; Induction for LH=Yes; Induction for RH=No; Inlet for LH=Yes; Inlet for RH=No; Length=40"; Q5A=18"; Q5B=20"; Q5Q=18"; Radius=4 15/16"; Width=40"
- ESTW 1/2-hp - 12L 1ROW COIL W/O S/ELBOW: Connector Bottom LH=Yes; Connector Bottom RH=No; Connector Top LH=Yes; Connector Top RH=No; Diameter=11 7/8"; Discharge Width "X"=20"; Duct Inlet Radius=6"; Elbow for LH=No; Elbow for RH=No; Enclosure for LH=Yes; Enclosure for RH=No; HWC Conn=0"; HWC Depth "Z"=12 1/4"; HWC for LH=Yes; HWC for RH=No; Height=18"; Induction Width "C"=17"; Induction for LH=Yes; Induction for RH=No; Inlet for LH=Yes; Inlet for RH=No; Length=40"; Q5A=18"; Q5B=20"; Q5Q=18"; Radius=5 15/16"; Width=40"
- ESTW 1/2-hp - 12R 1ROW COIL W/O S/ELBOW: Connector Bottom LH=No; Connector Bottom RH=Yes; Connector Top LH=No; Connector Top RH=Yes; Diameter=11 7/8"; Discharge Width "X"=20"; Duct Inlet Radius=6"; Elbow for LH=No; Elbow for RH=No; Enclosure for LH=No; Enclosure for RH=Yes; HWC Conn=0"; HWC Depth "Z"=12 1/4"; HWC for LH=No; HWC for RH=Yes; Height=18"; Induction Width "C"=17"; Induction for LH=No; Induction for RH=Yes; Inlet for LH=No; Inlet for RH=Yes; Length=40"; Q5A=18"; Q5B=20"; Q5Q=18"; Radius=5 15/16"; Width=40"
- ESTW 1/2-hp - 12L 1ROW COIL WITH S/ELBOW: Connector Bottom LH=Yes; Connector Bottom RH=No; Connector Top LH=Yes; Connector Top RH=No; Diameter=11 7/8"; Discharge Width "X"=20"; Duct Inlet Radius=6"; Elbow for LH=Yes; Elbow for RH=No; Enclosure for LH=Yes; Enclosure for RH=No; HWC Conn=0"; HWC Depth "Z"=12 1/4"; HWC for LH=Yes; HWC for RH=No; Height=18"; Induction Width "C"=17"; Induction for LH=Yes; Induction for RH=No; Inlet for LH=Yes; Inlet for RH=No; Length=40"; Q5A=18"; Q5B=20"; Q5Q=18"; Radius=5 15/16"; Width=40"
- ESTW 1/2-hp - 12R 1ROW COIL WITH S/ELBOW: Connector Bottom LH=No; Connector Bottom RH=Yes; Connector Top LH=No; Connector Top RH=Yes; Diameter=11 7/8"; Discharge Width "X"=20"; Duct Inlet Radius=6"; Elbow for LH=No; Elbow for RH=Yes; Enclosure for LH=No; Enclosure for RH=Yes; HWC Conn=0"; HWC Depth "Z"=12 1/4"; HWC for LH=No; HWC for RH=Yes; Height=18"; Induction Width "C"=17"; Induction for LH=No; Induction for RH=Yes; Inlet for LH=No; Inlet for RH=Yes; Length=40"; Q5A=18"; Q5B=20"; Q5Q=18"; Radius=5 15/16"; Width=40"
- ESTW 1/2-hp - 12L 2ROW COIL W/O S/ELBOW: Connector Bottom LH=Yes; Connector Bottom RH=No; Connector Top LH=Yes; Connector Top RH=No; Diameter=11 7/8"; Discharge Width "X"=20"; Duct Inlet Radius=6"; Elbow for LH=No; Elbow for RH=No; Enclosure for LH=Yes; Enclosure for RH=No; HWC Conn=0"; HWC Depth "Z"=13 1/2"; HWC for LH=Yes; HWC for RH=No; Height=18"; Induction Width "C"=17"; Induction for LH=Yes; Induction for RH=No; Inlet for LH=Yes; Inlet for RH=No; Length=40"; Q5A=18"; Q5B=20"; Q5Q=18"; Radius=5 15/16"; Width=40"
- ESTW 1/2-hp - 12R 2ROW COIL W/O S/ELBOW: Connector Bottom LH=No; Connector Bottom RH=Yes; Connector Top LH=No; Connector Top RH=Yes; Diameter=11 7/8"; Discharge Width "X"=20"; Duct Inlet Radius=6"; Elbow for LH=No; Elbow for RH=No; Enclosure for LH=No; Enclosure for RH=Yes; HWC Conn=0"; HWC Depth "Z"=13 1/2"; HWC for LH=No; HWC for RH=Yes; Height=18"; Induction Width "C"=17"; Induction for LH=No; Induction for RH=Yes; Inlet for LH=No; Inlet for RH=Yes; Length=40"; Q5A=18"; Q5B=20"; Q5Q=18"; Radius=5 15/16"; Width=40"
- ESTW 1/2-hp - 12R 2ROW COIL WITH S/ELBOW: Connector Bottom LH=No; Connector Bottom RH=Yes; Connector Top LH=No; Connector Top RH=Yes; Diameter=11 7/8"; Discharge Width "X"=20"; Duct Inlet Radius=6"; Elbow for LH=No; Elbow for RH=Yes; Enclosure for LH=No; Enclosure for RH=Yes; HWC Conn=0"; HWC Depth "Z"=13 1/2"; HWC for LH=No; HWC for RH=Yes; Height=18"; Induction Width "C"=17"; Induction for LH=No; Induction for RH=Yes; Inlet for LH=No; Inlet for RH=Yes; Length=40"; Q5A=18"; Q5B=20"; Q5Q=18"; Radius=5 15/16"; Width=40"
- ESTW 1/2-hp - 12L 2ROW COIL WITH S/ELBOW: Connector Bottom LH=Yes; Connector Bottom RH=No; Connector Top LH=Yes; Connector Top RH=No; Diameter=11 7/8"; Discharge Width "X"=20"; Duct Inlet Radius=6"; Elbow for LH=Yes; Elbow for RH=No; Enclosure for LH=No; Enclosure for RH=Yes; HWC Conn=0"; HWC Depth "Z"=13 1/2"; HWC for LH=No; HWC for RH=No; Height=18"; Induction Width "C"=17"; Induction for LH=Yes; Induction for RH=No; Inlet for LH=Yes; Inlet for RH=No; Length=40"; Q5A=18"; Q5B=20"; Q5Q=18"; Radius=5 15/16"; Width=40"
- ESTW 1/2-hp - 14L 1ROW COIL W/O S/ELBOW: Connector Bottom LH=Yes; Connector Bottom RH=No; Connector Top LH=Yes; Connector Top RH=No; Diameter=13 7/8"; Discharge Width "X"=20"; Duct Inlet Radius=7"; Elbow for LH=No; Elbow for RH=No; Enclosure for LH=Yes; Enclosure for RH=No; HWC Conn=0"; HWC Depth "Z"=12 1/4"; HWC for LH=Yes; HWC for RH=No; Height=18"; Induction Width "C"=17"; Induction for LH=Yes; Induction for RH=No; Inlet for LH=Yes; Inlet for RH=No; Length=40"; Q5A=18"; Q5B=20"; Q5Q=18"; Radius=6 15/16"; Width=40"
- ESTW 1/2-hp - 14R 1ROW COIL W/O S/ELBOW: Connector Bottom LH=No; Connector Bottom RH=Yes; Connector Top LH=No; Connector Top RH=Yes; Diameter=13 7/8"; Discharge Width "X"=20"; Duct Inlet Radius=7"; Elbow for LH=No; Elbow for RH=No; Enclosure for LH=No; Enclosure for RH=Yes; HWC Conn=0"; HWC Depth "Z"=12 1/4"; HWC for LH=No; HWC for RH=Yes; Height=18"; Induction Width "C"=17"; Induction for LH=No; Induction for RH=Yes; Inlet for LH=No; Inlet for RH=Yes; Length=40"; Q5A=18"; Q5B=20"; Q5Q=18"; Radius=6 15/16"; Width=40"
- ESTW 1/2-hp - 14R 1ROW COIL WITH S/ELBOW: Connector Bottom LH=No; Connector Bottom RH=Yes; Connector Top LH=No; Connector Top RH=Yes; Diameter=13 7/8"; Discharge Width "X"=20"; Duct Inlet Radius=7"; Elbow for LH=No; Elbow for RH=Yes; Enclosure for LH=No; Enclosure for RH=Yes; HWC Conn=0"; HWC Depth "Z"=12 1/4"; HWC for LH=No; HWC for RH=Yes; Height=18"; Induction Width "C"=17"; Induction for LH=No; Induction for RH=Yes; Inlet for LH=No; Inlet for RH=Yes; Length=40"; Q5A=18"; Q5B=20"; Q5Q=18"; Radius=6 15/16"; Width=40"
- ESTW 1/2-hp - 14L 1ROW COIL WITH S/ELBOW: Connector Bottom LH=Yes; Connector Bottom RH=No; Connector Top LH=Yes; Connector Top RH=No; Diameter=13 7/8"; Discharge Width "X"=20"; Duct Inlet Radius=7"; Elbow for LH=Yes; Elbow for RH=No; Enclosure for LH=Yes; Enclosure for RH=No; HWC Conn=0"; HWC Depth "Z"=12 1/4"; HWC for LH=Yes; HWC for RH=No; Height=18"; Induction Width "C"=17"; Induction for LH=Yes; Induction for RH=No; Inlet for LH=Yes; Inlet for RH=No; Length=40"; Q5A=18"; Q5B=20"; Q5Q=18"; Radius=6 15/16"; Width=40"
- ESTW 1/2-hp - 14L 2ROW COIL W/O S/ELBOW: Connector Bottom LH=Yes; Connector Bottom RH=No; Connector Top LH=Yes; Connector Top RH=No; Diameter=13 7/8"; Discharge Width "X"=20"; Duct Inlet Radius=7"; Elbow for LH=No; Elbow for RH=No; Enclosure for LH=Yes; Enclosure for RH=No; HWC Conn=0"; HWC Depth "Z"=13 1/2"; HWC for LH=Yes; HWC for RH=No; Height=18"; Induction Width "C"=17"; Induction for LH=Yes; Induction for RH=No; Inlet for LH=Yes; Inlet for RH=No; Length=40"; Q5A=18"; Q5B=20"; Q5Q=18"; Radius=6 15/16"; Width=40"
- ESTW 1/2-hp - 14R 2ROW COIL W/O S/ELBOW: Connector Bottom LH=No; Connector Bottom RH=Yes; Connector Top LH=No; Connector Top RH=Yes; Diameter=13 7/8"; Discharge Width "X"=20"; Duct Inlet Radius=7"; Elbow for LH=No; Elbow for RH=No; Enclosure for LH=No; Enclosure for RH=Yes; HWC Conn=0"; HWC Depth "Z"=13 1/2"; HWC for LH=No; HWC for RH=Yes; Height=18"; Induction Width "C"=17"; Induction for LH=No; Induction for RH=Yes; Inlet for LH=No; Inlet for RH=Yes; Length=40"; Q5A=18"; Q5B=20"; Q5Q=18"; Radius=6 15/16"; Width=40"
- ESTW 1/2-hp - 14L 2ROW COIL WITH S/ELBOW: Connector Bottom LH=Yes; Connector Bottom RH=No; Connector Top LH=Yes; Connector Top RH=No; Diameter=13 7/8"; Discharge Width "X"=20"; Duct Inlet Radius=7"; Elbow for LH=Yes; Elbow for RH=No; Enclosure for LH=Yes; Enclosure for RH=No; HWC Conn=0"; HWC Depth "Z"=13 1/2"; HWC for LH=Yes; HWC for RH=No; Height=18"; Induction Width "C"=17"; Induction for LH=Yes; Induction for RH=No; Inlet for LH=Yes; Inlet for RH=No; Length=40"; Q5A=18"; Q5B=20"; Q5Q=18"; Radius=6 15/16"; Width=40"
- ESTW 1/2-hp - 14R 2ROW COIL WITH S/ELBOW: Connector Bottom LH=No; Connector Bottom RH=Yes; Connector Top LH=No; Connector Top RH=Yes; Diameter=13 7/8"; Discharge Width "X"=20"; Duct Inlet Radius=7"; Elbow for LH=No; Elbow for RH=Yes; Enclosure for LH=No; Enclosure for RH=Yes; HWC Conn=0"; HWC Depth "Z"=13 1/2"; HWC for LH=No; HWC for RH=Yes; Height=18"; Induction Width "C"=17"; Induction for LH=No; Induction for RH=Yes; Inlet for LH=No; Inlet for RH=Yes; Length=40"; Q5A=18"; Q5B=20"; Q5Q=18"; Radius=6 15/16"; Width=40"
- ESTW 1-hp - 09L 1ROW COIL WITH S/ELBOW: Connector Bottom LH=Yes; Connector Bottom RH=No; Connector Top LH=Yes; Connector Top RH=No; Diameter=8 7/8"; Discharge Width "X"=24"; Duct Inlet Radius=4"; Elbow for LH=Yes; Elbow for RH=No; Enclosure for LH=Yes; Enclosure for RH=No; HWC Conn=0"; HWC Depth "Z"=12 1/4"; HWC for LH=Yes; HWC for RH=No; Height=20"; Induction Width "C"=21"; Induction for LH=Yes; Induction for RH=No; Inlet for LH=Yes; Inlet for RH=No; Length=48"; Q5A=20"; Q5B=24"; Q5Q=20"; Radius=4 7/16"; Width=48"
- ESTW 1-hp - 09R 1ROW COIL WITH S/ELBOW: Connector Bottom LH=No; Connector Bottom RH=Yes; Connector Top LH=No; Connector Top RH=Yes; Diameter=8 7/8"; Discharge Width "X"=24"; Duct Inlet Radius=4"; Elbow for LH=No; Elbow for RH=Yes; Enclosure for LH=No; Enclosure for RH=Yes; HWC Conn=0"; HWC Depth "Z"=12 1/4"; HWC for LH=No; HWC for RH=Yes; Height=20"; Induction Width "C"=21"; Induction for LH=No; Induction for RH=Yes; Inlet for LH=No; Inlet for RH=Yes; Length=48"; Q5A=20"; Q5B=24"; Q5Q=20"; Radius=4 7/16"; Width=48"
- ESTW 1-hp - 16R 2ROW COIL WITH S/ELBOW: Connector Bottom LH=No; Connector Bottom RH=Yes; Connector Top LH=No; Connector Top RH=Yes; Diameter=15 7/8"; Discharge Width "X"=24"; Duct Inlet Radius=8"; Elbow for LH=No; Elbow for RH=Yes; Enclosure for LH=No; Enclosure for RH=Yes; HWC Conn=0"; HWC Depth "Z"=13 1/2"; HWC for LH=No; HWC for RH=Yes; Height=20"; Induction Width "C"=21"; Induction for LH=No; Induction for RH=Yes; Inlet for LH=No; Inlet for RH=Yes; Length=48"; Q5A=20"; Q5B=24"; Q5Q=20"; Radius=7 15/16"; Width=48"
- ESTW 1-hp - 16L 2ROW COIL WITH S/ELBOW: Connector Bottom LH=Yes; Connector Bottom RH=No; Connector Top LH=Yes; Connector Top RH=No; Diameter=15 7/8"; Discharge Width "X"=24"; Duct Inlet Radius=8"; Elbow for LH=Yes; Elbow for RH=No; Enclosure for LH=Yes; Enclosure for RH=No; HWC Conn=0"; HWC Depth "Z"=13 1/2"; HWC for LH=Yes; HWC for RH=No; Height=20"; Induction Width "C"=21"; Induction for LH=Yes; Induction for RH=No; Inlet for LH=Yes; Inlet for RH=No; Length=48"; Q5A=20"; Q5B=24"; Q5Q=20"; Radius=7 15/16"; Width=48"
- ESTW 1-hp - 14L 2ROW COIL W/O S/ELBOW: Connector Bottom LH=Yes; Connector Bottom RH=No; Connector Top LH=Yes; Connector Top RH=No; Diameter=13 7/8"; Discharge Width "X"=24"; Duct Inlet Radius=7"; Elbow for LH=No; Elbow for RH=No; Enclosure for LH=Yes; Enclosure for RH=No; HWC Conn=0"; HWC Depth "Z"=13 1/2"; HWC for LH=Yes; HWC for RH=No; Height=20"; Induction Width "C"=21"; Induction for LH=Yes; Induction for RH=No; Inlet for LH=Yes; Inlet for RH=No; Length=48"; Q5A=20"; Q5B=24"; Q5Q=20"; Radius=6 15/16"; Width=48"
- ESTW 1-hp - 14R 2ROW COIL W/O S/ELBOW: Connector Bottom LH=No; Connector Bottom RH=Yes; Connector Top LH=No; Connector Top RH=Yes; Diameter=13 7/8"; Discharge Width "X"=24"; Duct Inlet Radius=7"; Elbow for LH=No; Elbow for RH=No; Enclosure for LH=No; Enclosure for RH=Yes; HWC Conn=0"; HWC Depth "Z"=13 1/2"; HWC for LH=No; HWC for RH=Yes; Height=20"; Induction Width "C"=21"; Induction for LH=No; Induction for RH=Yes; Inlet for LH=No; Inlet for RH=Yes; Length=48"; Q5A=20"; Q5B=24"; Q5Q=20"; Radius=6 15/16"; Width=48"
- ESTW 1-hp - 14R 2ROW COIL WITH S/ELBOW: Connector Bottom LH=No; Connector Bottom RH=Yes; Connector Top LH=No; Connector Top RH=Yes; Diameter=13 7/8"; Discharge Width "X"=24"; Duct Inlet Radius=7"; Elbow for LH=No; Elbow for RH=Yes; Enclosure for LH=No; Enclosure for RH=Yes; HWC Conn=0"; HWC Depth "Z"=13 1/2"; HWC for LH=No; HWC for RH=Yes; Height=20"; Induction Width "C"=21"; Induction for LH=No; Induction for RH=Yes; Inlet for LH=No; Inlet for RH=Yes; Length=48"; Q5A=20"; Q5B=24"; Q5Q=20"; Radius=6 15/16"; Width=48"
- ESTW 1-hp - 14L 2ROW COIL WITH S/ELBOW: Connector Bottom LH=Yes; Connector Bottom RH=No; Connector Top LH=Yes; Connector Top RH=No; Diameter=13 7/8"; Discharge Width "X"=24"; Duct Inlet Radius=7"; Elbow for LH=Yes; Elbow for RH=No; Enclosure for LH=Yes; Enclosure for RH=No; HWC Conn=0"; HWC Depth "Z"=13 1/2"; HWC for LH=Yes; HWC for RH=No; Height=20"; Induction Width "C"=21"; Induction for LH=Yes; Induction for RH=No; Inlet for LH=Yes; Inlet for RH=No; Length=48"; Q5A=20"; Q5B=24"; Q5Q=20"; Radius=6 15/16"; Width=48"
- ESTW 1-hp - 12L 2ROW COIL W/O S/ELBOW: Connector Bottom LH=Yes; Connector Bottom RH=No; Connector Top LH=Yes; Connector Top RH=No; Diameter=11 7/8"; Discharge Width "X"=24"; Duct Inlet Radius=6"; Elbow for LH=No; Elbow for RH=No; Enclosure for LH=Yes; Enclosure for RH=No; HWC Conn=0"; HWC Depth "Z"=13 1/2"; HWC for LH=Yes; HWC for RH=No; Height=20"; Induction Width "C"=21"; Induction for LH=Yes; Induction for RH=No; Inlet for LH=Yes; Inlet for RH=No; Length=48"; Q5A=20"; Q5B=24"; Q5Q=20"; Radius=5 15/16"; Width=48"
- ESTW 1-hp - 12R 2ROW COIL W/O S/ELBOW: Connector Bottom LH=No; Connector Bottom RH=Yes; Connector Top LH=No; Connector Top RH=Yes; Diameter=11 7/8"; Discharge Width "X"=24"; Duct Inlet Radius=6"; Elbow for LH=No; Elbow for RH=No; Enclosure for LH=No; Enclosure for RH=Yes; HWC Conn=0"; HWC Depth "Z"=13 1/2"; HWC for LH=No; HWC for RH=Yes; Height=20"; Induction Width "C"=21"; Induction for LH=Yes; Induction for RH=Yes; Inlet for LH=No; Inlet for RH=Yes; Length=48"; Q5A=20"; Q5B=24"; Q5Q=20"; Radius=5 15/16"; Width=48"
- ESTW 1-hp - 12R 2ROW COIL WITH S/ELBOW: Connector Bottom LH=No; Connector Bottom RH=Yes; Connector Top LH=No; Connector Top RH=Yes; Diameter=11 7/8"; Discharge Width "X"=24"; Duct Inlet Radius=6"; Elbow for LH=No; Elbow for RH=Yes; Enclosure for LH=No; Enclosure for RH=Yes; HWC Conn=0"; HWC Depth "Z"=13 1/2"; HWC for LH=No; HWC for RH=Yes; Height=20"; Induction Width "C"=21"; Induction for LH=Yes; Induction for RH=Yes; Inlet for LH=No; Inlet for RH=Yes; Length=48"; Q5A=20"; Q5B=24"; Q5Q=20"; Radius=5 15/16"; Width=48"
- ESTW 1-hp - 12L 2ROW COIL WITH S/ELBOW: Connector Bottom LH=Yes; Connector Bottom RH=No; Connector Top LH=Yes; Connector Top RH=No; Diameter=11 7/8"; Discharge Width "X"=24"; Duct Inlet Radius=6"; Elbow for LH=Yes; Elbow for RH=No; Enclosure for LH=Yes; Enclosure for RH=No; HWC Conn=0"; HWC Depth "Z"=13 1/2"; HWC for LH=Yes; HWC for RH=No; Height=20"; Induction Width "C"=21"; Induction for LH=Yes; Induction for RH=No; Inlet for LH=Yes; Inlet for RH=No; Length=48"; Q5A=20"; Q5B=24"; Q5Q=20"; Radius=5 15/16"; Width=48"
- ESTW 1-hp - 10L 2ROW COIL W/O S/ELBOW: Connector Bottom LH=Yes; Connector Bottom RH=No; Connector Top LH=Yes; Connector Top RH=No; Diameter=9 7/8"; Discharge Width "X"=24"; Duct Inlet Radius=5"; Elbow for LH=No; Elbow for RH=No; Enclosure for LH=Yes; Enclosure for RH=No; HWC Conn=0"; HWC Depth "Z"=13 1/2"; HWC for LH=Yes; HWC for RH=No; Height=20"; Induction Width "C"=21"; Induction for LH=Yes; Induction for RH=No; Inlet for LH=Yes; Inlet for RH=No; Length=48"; Q5A=20"; Q5B=24"; Q5Q=20"; Radius=4 15/16"; Width=48"
- ESTW 1-hp - 10R 2ROW COIL W/O S/ELBOW: Connector Bottom LH=No; Connector Bottom RH=Yes; Connector Top LH=No; Connector Top RH=Yes; Diameter=9 7/8"; Discharge Width "X"=24"; Duct Inlet Radius=5"; Elbow for LH=No; Elbow for RH=No; Enclosure for LH=No; Enclosure for RH=Yes; HWC Conn=0"; HWC Depth "Z"=13 1/2"; HWC for LH=No; HWC for RH=Yes; Height=20"; Induction Width "C"=21"; Induction for LH=No; Induction for RH=Yes; Inlet for LH=No; Inlet for RH=Yes; Length=48"; Q5A=20"; Q5B=24"; Q5Q=20"; Radius=4 15/16"; Width=48"
- ESTW 1-hp - 10R 2ROW COIL WITH S/ELBOW: Connector Bottom LH=No; Connector Bottom RH=Yes; Connector Top LH=No; Connector Top RH=Yes; Diameter=9 7/8"; Discharge Width "X"=24"; Duct Inlet Radius=5"; Elbow for LH=No; Elbow for RH=Yes; Enclosure for LH=No; Enclosure for RH=Yes; HWC Conn=0"; HWC Depth "Z"=13 1/2"; HWC for LH=No; HWC for RH=Yes; Height=20"; Induction Width "C"=21"; Induction for LH=No; Induction for RH=Yes; Inlet for LH=No; Inlet for RH=Yes; Length=48"; Q5A=20"; Q5B=24"; Q5Q=20"; Radius=4 15/16"; Width=48"
- ESTW 1-hp - 10L 2ROW COIL WITH S/ELBOW: Connector Bottom LH=Yes; Connector Bottom RH=No; Connector Top LH=Yes; Connector Top RH=No; Diameter=9 7/8"; Discharge Width "X"=24"; Duct Inlet Radius=5"; Elbow for LH=Yes; Elbow for RH=No; Enclosure for LH=Yes; Enclosure for RH=No; HWC Conn=0"; HWC Depth "Z"=13 1/2"; HWC for LH=Yes; HWC for RH=No; Height=20"; Induction Width "C"=21"; Induction for LH=Yes; Induction for RH=No; Inlet for LH=Yes; Inlet for RH=No; Length=48"; Q5A=20"; Q5B=24"; Q5Q=20"; Radius=4 15/16"; Width=48"
- ESTW 1-hp - 10L 1ROW COIL W/O S/ELBOW: Connector Bottom LH=Yes; Connector Bottom RH=No; Connector Top LH=Yes; Connector Top RH=No; Diameter=9 7/8"; Discharge Width "X"=24"; Duct Inlet Radius=5"; Elbow for LH=No; Elbow for RH=No; Enclosure for LH=Yes; Enclosure for RH=No; HWC Conn=0"; HWC Depth "Z"=12 1/4"; HWC for LH=Yes; HWC for RH=No; Height=20"; Induction Width "C"=21"; Induction for LH=Yes; Induction for RH=No; Inlet for LH=Yes; Inlet for RH=No; Length=48"; Q5A=20"; Q5B=24"; Q5Q=20"; Radius=4 15/16"; Width=48"
- ESTW 1-hp - 10R 1ROW COIL W/O S/ELBOW: Connector Bottom LH=No; Connector Bottom RH=Yes; Connector Top LH=No; Connector Top RH=Yes; Diameter=9 7/8"; Discharge Width "X"=24"; Duct Inlet Radius=5"; Elbow for LH=No; Elbow for RH=No; Enclosure for LH=No; Enclosure for RH=Yes; HWC Conn=0"; HWC Depth "Z"=12 1/4"; HWC for LH=No; HWC for RH=Yes; Height=20"; Induction Width "C"=21"; Induction for LH=No; Induction for RH=Yes; Inlet for LH=No; Inlet for RH=Yes; Length=48"; Q5A=20"; Q5B=24"; Q5Q=20"; Radius=4 15/16"; Width=48"
- ESTW 1-hp - 10R 1ROW COIL WITH S/ELBOW: Connector Bottom LH=No; Connector Bottom RH=Yes; Connector Top LH=No; Connector Top RH=Yes; Diameter=9 7/8"; Discharge Width "X"=24"; Duct Inlet Radius=5"; Elbow for LH=No; Elbow for RH=Yes; Enclosure for LH=No; Enclosure for RH=Yes; HWC Conn=0"; HWC Depth "Z"=12 1/4"; HWC for LH=No; HWC for RH=Yes; Height=20"; Induction Width "C"=21"; Induction for LH=No; Induction for RH=Yes; Inlet for LH=No; Inlet for RH=Yes; Length=48"; Q5A=20"; Q5B=24"; Q5Q=20"; Radius=4 15/16"; Width=48"
- ESTW 1-hp - 10L 1ROW COIL WITH S/ELBOW: Connector Bottom LH=Yes; Connector Bottom RH=No; Connector Top LH=Yes; Connector Top RH=No; Diameter=9 7/8"; Discharge Width "X"=24"; Duct Inlet Radius=5"; Elbow for LH=Yes; Elbow for RH=No; Enclosure for LH=Yes; Enclosure for RH=No; HWC Conn=0"; HWC Depth "Z"=12 1/4"; HWC for LH=Yes; HWC for RH=No; Height=20"; Induction Width "C"=21"; Induction for LH=Yes; Induction for RH=No; Inlet for LH=Yes; Inlet for RH=No; Length=48"; Q5A=20"; Q5B=24"; Q5Q=20"; Radius=4 15/16"; Width=48"
- ESTW 1-hp - 12L 1ROW COIL W/O S/ELBOW: Connector Bottom LH=Yes; Connector Bottom RH=No; Connector Top LH=Yes; Connector Top RH=No; Diameter=11 7/8"; Discharge Width "X"=24"; Duct Inlet Radius=6"; Elbow for LH=No; Elbow for RH=No; Enclosure for LH=Yes; Enclosure for RH=No; HWC Conn=0"; HWC Depth "Z"=12 1/4"; HWC for LH=Yes; HWC for RH=No; Height=20"; Induction Width "C"=21"; Induction for LH=Yes; Induction for RH=No; Inlet for LH=Yes; Inlet for RH=No; Length=48"; Q5A=20"; Q5B=24"; Q5Q=20"; Radius=5 15/16"; Width=48"
- ESTW 1-hp - 12R 1ROW COIL W/O S/ELBOW: Connector Bottom LH=No; Connector Bottom RH=Yes; Connector Top LH=No; Connector Top RH=Yes; Diameter=11 7/8"; Discharge Width "X"=24"; Duct Inlet Radius=6"; Elbow for LH=No; Elbow for RH=No; Enclosure for LH=No; Enclosure for RH=Yes; HWC Conn=0"; HWC Depth "Z"=12 1/4"; HWC for LH=No; HWC for RH=Yes; Height=20"; Induction Width "C"=21"; Induction for LH=No; Induction for RH=Yes; Inlet for LH=No; Inlet for RH=Yes; Length=48"; Q5A=20"; Q5B=24"; Q5Q=20"; Radius=5 15/16"; Width=48"
- ESTW 1-hp - 12R 1ROW COIL WITH S/ELBOW: Connector Bottom LH=No; Connector Bottom RH=Yes; Connector Top LH=No; Connector Top RH=Yes; Diameter=11 7/8"; Discharge Width "X"=24"; Duct Inlet Radius=6"; Elbow for LH=No; Elbow for RH=Yes; Enclosure for LH=No; Enclosure for RH=Yes; HWC Conn=0"; HWC Depth "Z"=12 1/4"; HWC for LH=No; HWC for RH=Yes; Height=20"; Induction Width "C"=21"; Induction for LH=No; Induction for RH=Yes; Inlet for LH=No; Inlet for RH=Yes; Length=48"; Q5A=20"; Q5B=24"; Q5Q=20"; Radius=5 15/16"; Width=48"
- ESTW 1-hp - 12L 1ROW COIL WITH S/ELBOW: Connector Bottom LH=Yes; Connector Bottom RH=No; Connector Top LH=Yes; Connector Top RH=No; Diameter=11 7/8"; Discharge Width "X"=24"; Duct Inlet Radius=6"; Elbow for LH=Yes; Elbow for RH=No; Enclosure for LH=Yes; Enclosure for RH=No; HWC Conn=0"; HWC Depth "Z"=12 1/4"; HWC for LH=Yes; HWC for RH=No; Height=20"; Induction Width "C"=21"; Induction for LH=Yes; Induction for RH=No; Inlet for LH=Yes; Inlet for RH=No; Length=48"; Q5A=20"; Q5B=24"; Q5Q=20"; Radius=5 15/16"; Width=48"
- ESTW 1-hp - 14L 1ROW COIL W/O S/ELBOW: Connector Bottom LH=Yes; Connector Bottom RH=No; Connector Top LH=Yes; Connector Top RH=No; Diameter=13 7/8"; Discharge Width "X"=24"; Duct Inlet Radius=7"; Elbow for LH=No; Elbow for RH=No; Enclosure for LH=Yes; Enclosure for RH=No; HWC Conn=0"; HWC Depth "Z"=12 1/4"; HWC for LH=Yes; HWC for RH=No; Height=20"; Induction Width "C"=21"; Induction for LH=Yes; Induction for RH=No; Inlet for LH=Yes; Inlet for RH=No; Length=48"; Q5A=20"; Q5B=24"; Q5Q=20"; Radius=6 15/16"; Width=48"
- ESTW 1-hp - 14R 1ROW COIL W/O S/ELBOW: Connector Bottom LH=No; Connector Bottom RH=Yes; Connector Top LH=No; Connector Top RH=Yes; Diameter=13 7/8"; Discharge Width "X"=24"; Duct Inlet Radius=7"; Elbow for LH=No; Elbow for RH=No; Enclosure for LH=No; Enclosure for RH=Yes; HWC Conn=0"; HWC Depth "Z"=12 1/4"; HWC for LH=No; HWC for RH=Yes; Height=20"; Induction Width "C"=21"; Induction for LH=No; Induction for RH=Yes; Inlet for LH=No; Inlet for RH=Yes; Length=48"; Q5A=20"; Q5B=24"; Q5Q=20"; Radius=6 15/16"; Width=48"
- ESTW 1-hp - 14R 1ROW COIL WITH S/ELBOW: Connector Bottom LH=No; Connector Bottom RH=Yes; Connector Top LH=No; Connector Top RH=Yes; Diameter=13 7/8"; Discharge Width "X"=24"; Duct Inlet Radius=7"; Elbow for LH=No; Elbow for RH=Yes; Enclosure for LH=No; Enclosure for RH=Yes; HWC Conn=0"; HWC Depth "Z"=12 1/4"; HWC for LH=No; HWC for RH=Yes; Height=20"; Induction Width "C"=21"; Induction for LH=No; Induction for RH=Yes; Inlet for LH=No; Inlet for RH=Yes; Length=48"; Q5A=20"; Q5B=24"; Q5Q=20"; Radius=6 15/16"; Width=48"
- ESTW 1-hp - 14L 1ROW COIL WITH S/ELBOW: Connector Bottom LH=Yes; Connector Bottom RH=No; Connector Top LH=Yes; Connector Top RH=No; Diameter=13 7/8"; Discharge Width "X"=24"; Duct Inlet Radius=7"; Elbow for LH=No; Elbow for RH=No; Enclosure for LH=Yes; Enclosure for RH=No; HWC Conn=0"; HWC Depth "Z"=12 1/4"; HWC for LH=Yes; HWC for RH=No; Height=20"; Induction Width "C"=21"; Induction for LH=Yes; Induction for RH=No; Inlet for LH=Yes; Inlet for RH=No; Length=48"; Q5A=20"; Q5B=24"; Q5Q=20"; Radius=6 15/16"; Width=48"
- ESTW 1-hp - 16L 1ROW COIL W/O S/ELBOW: Connector Bottom LH=Yes; Connector Bottom RH=No; Connector Top LH=Yes; Connector Top RH=No; Diameter=15 7/8"; Discharge Width "X"=24"; Duct Inlet Radius=8"; Elbow for LH=No; Elbow for RH=No; Enclosure for LH=Yes; Enclosure for RH=No; HWC Conn=0"; HWC Depth "Z"=12 1/4"; HWC for LH=Yes; HWC for RH=No; Height=20"; Induction Width "C"=21"; Induction for LH=Yes; Induction for RH=No; Inlet for LH=Yes; Inlet for RH=No; Length=48"; Q5A=20"; Q5B=24"; Q5Q=20"; Radius=7 15/16"; Width=48"
- ESTW 1-hp - 16R 1ROW COIL W/O S/ELBOW: Connector Bottom LH=No; Connector Bottom RH=Yes; Connector Top LH=No; Connector Top RH=Yes; Diameter=15 7/8"; Discharge Width "X"=24"; Duct Inlet Radius=8"; Elbow for LH=No; Elbow for RH=No; Enclosure for LH=No; Enclosure for RH=Yes; HWC Conn=0"; HWC Depth "Z"=12 1/4"; HWC for LH=No; HWC for RH=Yes; Height=20"; Induction Width "C"=21"; Induction for LH=No; Induction for RH=Yes; Inlet for LH=No; Inlet for RH=Yes; Length=48"; Q5A=20"; Q5B=24"; Q5Q=20"; Radius=7 15/16"; Width=48"
- ESTW 1-hp - 16R 1ROW COIL WITH S/ELBOW: Connector Bottom LH=No; Connector Bottom RH=Yes; Connector Top LH=No; Connector Top RH=Yes; Diameter=15 7/8"; Discharge Width "X"=24"; Duct Inlet Radius=8"; Elbow for LH=No; Elbow for RH=Yes; Enclosure for LH=No; Enclosure for RH=Yes; HWC Conn=0"; HWC Depth "Z"=12 1/4"; HWC for LH=No; HWC for RH=Yes; Height=20"; Induction Width "C"=21"; Induction for LH=No; Induction for RH=Yes; Inlet for LH=No; Inlet for RH=Yes; Length=48"; Q5A=20"; Q5B=24"; Q5Q=20"; Radius=7 15/16"; Width=48"
- ESTW 1-hp - 16L 1ROW COIL WITH S/ELBOW: Connector Bottom LH=Yes; Connector Bottom RH=No; Connector Top LH=Yes; Connector Top RH=No; Diameter=15 7/8"; Discharge Width "X"=24"; Duct Inlet Radius=8"; Elbow for LH=Yes; Elbow for RH=No; Enclosure for LH=Yes; Enclosure for RH=No; HWC Conn=0"; HWC Depth "Z"=12 1/4"; HWC for LH=Yes; HWC for RH=No; Height=20"; Induction Width "C"=21"; Induction for LH=Yes; Induction for RH=No; Inlet for LH=Yes; Inlet for RH=No; Length=48"; Q5A=20"; Q5B=24"; Q5Q=20"; Radius=7 15/16"; Width=48"
- ESTW 3/4-hp - 08L 1ROW COIL W/O S/ELBOW: Connector Bottom LH=Yes; Connector Bottom RH=No; Connector Top LH=Yes; Connector Top RH=No; Diameter=7 7/8"; Discharge Width "X"=24"; Duct Inlet Radius=4"; Elbow for LH=No; Elbow for RH=No; Enclosure for LH=Yes; Enclosure for RH=No; HWC Conn=0"; HWC Depth "Z"=12 1/4"; HWC for LH=Yes; HWC for RH=No; Height=20"; Induction Width "C"=21"; Induction for LH=Yes; Induction for RH=No; Inlet for LH=Yes; Inlet for RH=No; Length=48"; Q5A=20"; Q5B=24"; Q5Q=20"; Radius=3 15/16"; Width=48"
- ESTW 3/4-hp - 08R 1ROW COIL W/O S/ELBOW: Connector Bottom LH=No; Connector Bottom RH=Yes; Connector Top LH=No; Connector Top RH=Yes; Diameter=7 7/8"; Discharge Width "X"=24"; Duct Inlet Radius=4"; Elbow for LH=No; Elbow for RH=No; Enclosure for LH=No; Enclosure for RH=Yes; HWC Conn=0"; HWC Depth "Z"=12 1/4"; HWC for LH=No; HWC for RH=Yes; Height=20"; Induction Width "C"=21"; Induction for LH=No; Induction for RH=Yes; Inlet for LH=No; Inlet for RH=Yes; Length=48"; Q5A=20"; Q5B=24"; Q5Q=20"; Radius=3 15/16"; Width=48"
- ESTW 3/4-hp - 08R 1ROW COIL WITH S/ELBOW: Connector Bottom LH=No; Connector Bottom RH=Yes; Connector Top LH=No; Connector Top RH=Yes; Diameter=7 7/8"; Discharge Width "X"=24"; Duct Inlet Radius=4"; Elbow for LH=No; Elbow for RH=Yes; Enclosure for LH=No; Enclosure for RH=Yes; HWC Conn=0"; HWC Depth "Z"=12 1/4"; HWC for LH=No; HWC for RH=Yes; Height=20"; Induction Width "C"=21"; Induction for LH=No; Induction for RH=Yes; Inlet for LH=No; Inlet for RH=Yes; Length=48"; Q5A=20"; Q5B=24"; Q5Q=20"; Radius=3 15/16"; Width=48"
- ESTW 3/4-hp - 08L 1ROW COIL WITH S/ELBOW: Connector Bottom LH=Yes; Connector Bottom RH=No; Connector Top LH=Yes; Connector Top RH=No; Diameter=7 7/8"; Discharge Width "X"=24"; Duct Inlet Radius=4"; Elbow for LH=Yes; Elbow for RH=No; Enclosure for LH=Yes; Enclosure for RH=No; HWC Conn=0"; HWC Depth "Z"=12 1/4"; HWC for LH=Yes; HWC for RH=No; Height=20"; Induction Width "C"=21"; Induction for LH=Yes; Induction for RH=No; Inlet for LH=Yes; Inlet for RH=No; Length=48"; Q5A=20"; Q5B=24"; Q5Q=20"; Radius=3 15/16"; Width=48"
- ESTW 3/4-hp - 08L 2ROW COIL W/O S/ELBOW: Connector Bottom LH=Yes; Connector Bottom RH=No; Connector Top LH=Yes; Connector Top RH=No; Diameter=7 7/8"; Discharge Width "X"=24"; Duct Inlet Radius=4"; Elbow for LH=No; Elbow for RH=No; Enclosure for LH=Yes; Enclosure for RH=No; HWC Conn=0"; HWC Depth "Z"=13 1/2"; HWC for LH=Yes; HWC for RH=No; Height=20"; Induction Width "C"=21"; Induction for LH=Yes; Induction for RH=No; Inlet for LH=Yes; Inlet for RH=No; Length=48"; Q5A=20"; Q5B=24"; Q5Q=20"; Radius=3 15/16"; Width=48"
- ESTW 3/4-hp - 08R 2ROW COIL W/O S/ELBOW: Connector Bottom LH=No; Connector Bottom RH=Yes; Connector Top LH=No; Connector Top RH=Yes; Diameter=7 7/8"; Discharge Width "X"=24"; Duct Inlet Radius=4"; Elbow for LH=No; Elbow for RH=No; Enclosure for LH=No; Enclosure for RH=Yes; HWC Conn=0"; HWC Depth "Z"=13 1/2"; HWC for LH=No; HWC for RH=Yes; Height=20"; Induction Width "C"=21"; Induction for LH=No; Induction for RH=Yes; Inlet for LH=No; Inlet for RH=Yes; Length=48"; Q5A=20"; Q5B=24"; Q5Q=20"; Radius=3 15/16"; Width=48"
- ESTW 3/4-hp - 08R 2ROW COIL WITH S/ELBOW: Connector Bottom LH=No; Connector Bottom RH=Yes; Connector Top LH=No; Connector Top RH=Yes; Diameter=7 7/8"; Discharge Width "X"=24"; Duct Inlet Radius=4"; Elbow for LH=No; Elbow for RH=Yes; Enclosure for LH=No; Enclosure for RH=Yes; HWC Conn=0"; HWC Depth "Z"=13 1/2"; HWC for LH=No; HWC for RH=Yes; Height=20"; Induction Width "C"=21"; Induction for LH=No; Induction for RH=Yes; Inlet for LH=No; Inlet for RH=Yes; Length=48"; Q5A=20"; Q5B=24"; Q5Q=20"; Radius=3 15/16"; Width=48"
- ESTW 3/4-hp - 08L 2ROW COIL WITH S/ELBOW: Connector Bottom LH=Yes; Connector Bottom RH=No; Connector Top LH=Yes; Connector Top RH=No; Diameter=7 7/8"; Discharge Width "X"=24"; Duct Inlet Radius=4"; Elbow for LH=Yes; Elbow for RH=No; Enclosure for LH=Yes; Enclosure for RH=No; HWC Conn=0"; HWC Depth "Z"=13 1/2"; HWC for LH=Yes; HWC for RH=No; Height=20"; Induction Width "C"=21"; Induction for LH=Yes; Induction for RH=No; Inlet for LH=Yes; Inlet for RH=No; Length=48"; Q5A=20"; Q5B=24"; Q5Q=20"; Radius=3 15/16"; Width=48"
- ESTW 3/4-hp - 07L 1ROW COIL W/O S/ELBOW: Connector Bottom LH=Yes; Connector Bottom RH=No; Connector Top LH=Yes; Connector Top RH=No; Diameter=6 7/8"; Discharge Width "X"=24"; Duct Inlet Radius=3"; Elbow for LH=No; Elbow for RH=No; Enclosure for LH=Yes; Enclosure for RH=No; HWC Conn=0"; HWC Depth "Z"=12 1/4"; HWC for LH=Yes; HWC for RH=No; Height=20"; Induction Width "C"=21"; Induction for LH=Yes; Induction for RH=No; Inlet for LH=Yes; Inlet for RH=No; Length=48"; Q5A=20"; Q5B=24"; Q5Q=20"; Radius=3 7/16"; Width=48"
- ESTW 3/4-hp - 07R 1ROW COIL W/O S/ELBOW: Connector Bottom LH=No; Connector Bottom RH=Yes; Connector Top LH=No; Connector Top RH=Yes; Diameter=6 7/8"; Discharge Width "X"=24"; Duct Inlet Radius=3"; Elbow for LH=No; Elbow for RH=No; Enclosure for LH=No; Enclosure for RH=Yes; HWC Conn=0"; HWC Depth "Z"=12 1/4"; HWC for LH=No; HWC for RH=Yes; Height=20"; Induction Width "C"=21"; Induction for LH=No; Induction for RH=Yes; Inlet for LH=No; Inlet for RH=Yes; Length=48"; Q5A=20"; Q5B=24"; Q5Q=20"; Radius=3 7/16"; Width=48"
- ESTW 3/4-hp - 07R 1ROW COIL WITH S/ELBOW: Connector Bottom LH=No; Connector Bottom RH=Yes; Connector Top LH=No; Connector Top RH=Yes; Diameter=6 7/8"; Discharge Width "X"=24"; Duct Inlet Radius=3"; Elbow for LH=No; Elbow for RH=Yes; Enclosure for LH=No; Enclosure for RH=Yes; HWC Conn=0"; HWC Depth "Z"=12 1/4"; HWC for LH=No; HWC for RH=Yes; Height=20"; Induction Width "C"=21"; Induction for LH=No; Induction for RH=Yes; Inlet for LH=No; Inlet for RH=Yes; Length=48"; Q5A=20"; Q5B=24"; Q5Q=20"; Radius=3 7/16"; Width=48"
- ESTW 3/4-hp - 07L 1ROW COIL WITH S/ELBOW: Connector Bottom LH=Yes; Connector Bottom RH=No; Connector Top LH=Yes; Connector Top RH=No; Diameter=6 7/8"; Discharge Width "X"=24"; Duct Inlet Radius=3"; Elbow for LH=Yes; Elbow for RH=No; Enclosure for LH=Yes; Enclosure for RH=No; HWC Conn=0"; HWC Depth "Z"=12 1/4"; HWC for LH=Yes; HWC for RH=No; Height=20"; Induction Width "C"=21"; Induction for LH=Yes; Induction for RH=No; Inlet for LH=Yes; Inlet for RH=No; Length=48"; Q5A=20"; Q5B=24"; Q5Q=20"; Radius=3 7/16"; Width=48"
- ESTW 3/4-hp - 07L 2ROW COIL W/O S/ELBOW: Connector Bottom LH=Yes; Connector Bottom RH=No; Connector Top LH=Yes; Connector Top RH=No; Diameter=6 7/8"; Discharge Width "X"=24"; Duct Inlet Radius=3"; Elbow for LH=No; Elbow for RH=No; Enclosure for LH=Yes; Enclosure for RH=No; HWC Conn=0"; HWC Depth "Z"=13 1/2"; HWC for LH=Yes; HWC for RH=No; Height=20"; Induction Width "C"=21"; Induction for LH=Yes; Induction for RH=No; Inlet for LH=Yes; Inlet for RH=No; Length=48"; Q5A=20"; Q5B=24"; Q5Q=20"; Radius=3 7/16"; Width=48"
- ESTW 3/4-hp - 07R 2ROW COIL W/O S/ELBOW: Connector Bottom LH=No; Connector Bottom RH=Yes; Connector Top LH=No; Connector Top RH=Yes; Diameter=6 7/8"; Discharge Width "X"=24"; Duct Inlet Radius=3"; Elbow for LH=No; Elbow for RH=No; Enclosure for LH=No; Enclosure for RH=Yes; HWC Conn=0"; HWC Depth "Z"=13 1/2"; HWC for LH=No; HWC for RH=Yes; Height=20"; Induction Width "C"=21"; Induction for LH=No; Induction for RH=Yes; Inlet for LH=No; Inlet for RH=Yes; Length=48"; Q5A=20"; Q5B=24"; Q5Q=20"; Radius=3 7/16"; Width=48"
- ESTW 3/4-hp - 07R 2ROW COIL WITH S/ELBOW: Connector Bottom LH=No; Connector Bottom RH=Yes; Connector Top LH=No; Connector Top RH=Yes; Diameter=6 7/8"; Discharge Width "X"=24"; Duct Inlet Radius=3"; Elbow for LH=No; Elbow for RH=Yes; Enclosure for LH=No; Enclosure for RH=Yes; HWC Conn=0"; HWC Depth "Z"=13 1/2"; HWC for LH=No; HWC for RH=Yes; Height=20"; Induction Width "C"=21"; Induction for LH=No; Induction for RH=Yes; Inlet for LH=No; Inlet for RH=Yes; Length=48"; Q5A=20"; Q5B=24"; Q5Q=20"; Radius=3 7/16"; Width=48"
- ESTW 3/4-hp - 07L 2ROW COIL WITH S/ELBOW: Connector Bottom LH=Yes; Connector Bottom RH=No; Connector Top LH=Yes; Connector Top RH=No; Diameter=6 7/8"; Discharge Width "X"=24"; Duct Inlet Radius=3"; Elbow for LH=Yes; Elbow for RH=No; Enclosure for LH=Yes; Enclosure for RH=No; HWC Conn=0"; HWC Depth "Z"=13 1/2"; HWC for LH=Yes; HWC for RH=No; Height=20"; Induction Width "C"=21"; Induction for LH=Yes; Induction for RH=No; Inlet for LH=Yes; Inlet for RH=No; Length=48"; Q5A=20"; Q5B=24"; Q5Q=20"; Radius=3 7/16"; Width=48"
- ESTW 3/4-hp - 09L 1ROW COIL W/O S/ELBOW: Connector Bottom LH=Yes; Connector Bottom RH=No; Connector Top LH=Yes; Connector Top RH=No; Diameter=8 7/8"; Discharge Width "X"=24"; Duct Inlet Radius=4"; Elbow for LH=No; Elbow for RH=No; Enclosure for LH=Yes; Enclosure for RH=No; HWC Conn=0"; HWC Depth "Z"=12 1/4"; HWC for LH=Yes; HWC for RH=No; Height=20"; Induction Width "C"=21"; Induction for LH=Yes; Induction for RH=No; Inlet for LH=Yes; Inlet for RH=No; Length=48"; Q5A=20"; Q5B=24"; Q5Q=20"; Radius=4 7/16"; Width=48"
- ESTW 3/4-hp - 09R 1ROW COIL W/O S/ELBOW: Connector Bottom LH=No; Connector Bottom RH=Yes; Connector Top LH=No; Connector Top RH=Yes; Diameter=8 7/8"; Discharge Width "X"=24"; Duct Inlet Radius=4"; Elbow for LH=No; Elbow for RH=No; Enclosure for LH=No; Enclosure for RH=Yes; HWC Conn=0"; HWC Depth "Z"=12 1/4"; HWC for LH=No; HWC for RH=Yes; Height=20"; Induction Width "C"=21"; Induction for LH=No; Induction for RH=Yes; Inlet for LH=No; Inlet for RH=Yes; Length=48"; Q5A=20"; Q5B=24"; Q5Q=20"; Radius=4 7/16"; Width=48"
- ESTW 3/4-hp - 09R 1ROW COIL WITH S/ELBOW: Connector Bottom LH=No; Connector Bottom RH=Yes; Connector Top LH=No; Connector Top RH=Yes; Diameter=8 7/8"; Discharge Width "X"=24"; Duct Inlet Radius=4"; Elbow for LH=No; Elbow for RH=Yes; Enclosure for LH=No; Enclosure for RH=Yes; HWC Conn=0"; HWC Depth "Z"=12 1/4"; HWC for LH=No; HWC for RH=Yes; Height=20"; Induction Width "C"=21"; Induction for LH=No; Induction for RH=Yes; Inlet for LH=No; Inlet for RH=Yes; Length=48"; Q5A=20"; Q5B=24"; Q5Q=20"; Radius=4 7/16"; Width=48"
- ESTW 3/4-hp - 09L 1ROW COIL WITH S/ELBOW: Connector Bottom LH=Yes; Connector Bottom RH=No; Connector Top LH=Yes; Connector Top RH=No; Diameter=8 7/8"; Discharge Width "X"=24"; Duct Inlet Radius=4"; Elbow for LH=Yes; Elbow for RH=No; Enclosure for LH=Yes; Enclosure for RH=No; HWC Conn=0"; HWC Depth "Z"=12 1/4"; HWC for LH=Yes; HWC for RH=No; Height=20"; Induction Width "C"=21"; Induction for LH=Yes; Induction for RH=No; Inlet for LH=Yes; Inlet for RH=No; Length=48"; Q5A=20"; Q5B=24"; Q5Q=20"; Radius=4 7/16"; Width=48"
- ESTW 1-hp - 09L 2ROW COIL W/O S/ELBOW: Connector Bottom LH=Yes; Connector Bottom RH=No; Connector Top LH=Yes; Connector Top RH=No; Diameter=8 7/8"; Discharge Width "X"=24"; Duct Inlet Radius=4"; Elbow for LH=No; Elbow for RH=No; Enclosure for LH=Yes; Enclosure for RH=No; HWC Conn=0"; HWC Depth "Z"=13 1/2"; HWC for LH=Yes; HWC for RH=No; Height=20"; Induction Width "C"=21"; Induction for LH=Yes; Induction for RH=No; Inlet for LH=Yes; Inlet for RH=No; Length=48"; Q5A=20"; Q5B=24"; Q5Q=20"; Radius=4 7/16"; Width=48"
- ESTW 1-hp - 09R 2ROW COIL W/O S/ELBOW: Connector Bottom LH=No; Connector Bottom RH=Yes; Connector Top LH=No; Connector Top RH=Yes; Diameter=8 7/8"; Discharge Width "X"=24"; Duct Inlet Radius=4"; Elbow for LH=No; Elbow for RH=No; Enclosure for LH=No; Enclosure for RH=Yes; HWC Conn=0"; HWC Depth "Z"=13 1/2"; HWC for LH=No; HWC for RH=Yes; Height=20"; Induction Width "C"=21"; Induction for LH=No; Induction for RH=Yes; Inlet for LH=No; Inlet for RH=Yes; Length=48"; Q5A=20"; Q5B=24"; Q5Q=20"; Radius=4 7/16"; Width=48"
- ESTW 1-hp - 09L 2ROW COIL WITH S/ELBOW: Connector Bottom LH=Yes; Connector Bottom RH=No; Connector Top LH=Yes; Connector Top RH=No; Diameter=8 7/8"; Discharge Width "X"=24"; Duct Inlet Radius=4"; Elbow for LH=Yes; Elbow for RH=No; Enclosure for LH=Yes; Enclosure for RH=No; HWC Conn=0"; HWC Depth "Z"=13 1/2"; HWC for LH=Yes; HWC for RH=Yes; Height=20"; Induction Width "C"=21"; Induction for LH=Yes; Induction for RH=No; Inlet for LH=Yes; Inlet for RH=No; Length=48"; Q5A=20"; Q5B=24"; Q5Q=20"; Radius=4 7/16"; Width=48"
- ESTW 1-hp - 09R 2ROW COIL WITH S/ELBOW: Connector Bottom LH=No; Connector Bottom RH=Yes; Connector Top LH=No; Connector Top RH=Yes; Diameter=8 7/8"; Discharge Width "X"=24"; Duct Inlet Radius=4"; Elbow for LH=No; Elbow for RH=Yes; Enclosure for LH=No; Enclosure for RH=Yes; HWC Conn=0"; HWC Depth "Z"=13 1/2"; HWC for LH=No; HWC for RH=Yes; Height=20"; Induction Width "C"=21"; Induction for LH=No; Induction for RH=Yes; Inlet for LH=No; Inlet for RH=Yes; Length=48"; Q5A=20"; Q5B=24"; Q5Q=20"; Radius=4 7/16"; Width=48"
- ESTW 3/4-hp - 09R 2ROW COIL W/O S/ELBOW: Connector Bottom LH=No; Connector Bottom RH=Yes; Connector Top LH=No; Connector Top RH=Yes; Diameter=8 7/8"; Discharge Width "X"=24"; Duct Inlet Radius=4"; Elbow for LH=No; Elbow for RH=No; Enclosure for LH=No; Enclosure for RH=Yes; HWC Conn=0"; HWC Depth "Z"=13 1/2"; HWC for LH=No; HWC for RH=Yes; Height=20"; Induction Width "C"=21"; Induction for LH=No; Induction for RH=Yes; Inlet for LH=No; Inlet for RH=Yes; Length=48"; Q5A=20"; Q5B=24"; Q5Q=20"; Radius=4 7/16"; Width=48"
- ESTW 3/4-hp - 09L 2ROW COIL W/O S/ELBOW: Connector Bottom LH=Yes; Connector Bottom RH=No; Connector Top LH=Yes; Connector Top RH=No; Diameter=8 7/8"; Discharge Width "X"=24"; Duct Inlet Radius=4"; Elbow for LH=No; Elbow for RH=No; Enclosure for LH=Yes; Enclosure for RH=No; HWC Conn=0"; HWC Depth "Z"=13 1/2"; HWC for LH=Yes; HWC for RH=No; Height=20"; Induction Width "C"=21"; Induction for LH=Yes; Induction for RH=No; Inlet for LH=Yes; Inlet for RH=No; Length=48"; Q5A=20"; Q5B=24"; Q5Q=20"; Radius=4 7/16"; Width=48"
- ESTW 3/4-hp - 09L 2ROW COIL WITH S/ELBOW: Connector Bottom LH=Yes; Connector Bottom RH=No; Connector Top LH=Yes; Connector Top RH=No; Diameter=8 7/8"; Discharge Width "X"=24"; Duct Inlet Radius=4"; Elbow for LH=Yes; Elbow for RH=No; Enclosure for LH=Yes; Enclosure for RH=No; HWC Conn=0"; HWC Depth "Z"=13 1/2"; HWC for LH=Yes; HWC for RH=No; Height=20"; Induction Width "C"=21"; Induction for LH=Yes; Induction for RH=No; Inlet for LH=Yes; Inlet for RH=No; Length=48"; Q5A=20"; Q5B=24"; Q5Q=20"; Radius=4 7/16"; Width=48"
- ESTW 3/4-hp - 09R 2ROW COIL WITH S/ELBOW: Connector Bottom LH=No; Connector Bottom RH=Yes; Connector Top LH=No; Connector Top RH=Yes; Diameter=8 7/8"; Discharge Width "X"=24"; Duct Inlet Radius=4"; Elbow for LH=No; Elbow for RH=Yes; Enclosure for LH=No; Enclosure for RH=Yes; HWC Conn=0"; HWC Depth "Z"=13 1/2"; HWC for LH=No; HWC for RH=Yes; Height=20"; Induction Width "C"=21"; Induction for LH=No; Induction for RH=Yes; Inlet for LH=No; Inlet for RH=Yes; Length=48"; Q5A=20"; Q5B=24"; Q5Q=20"; Radius=4 7/16"; Width=48"
- ESTW 3/4-hp - 10L 1ROW COIL W/O S/ELBOW: Connector Bottom LH=Yes; Connector Bottom RH=No; Connector Top LH=Yes; Connector Top RH=No; Diameter=9 7/8"; Discharge Width "X"=24"; Duct Inlet Radius=5"; Elbow for LH=No; Elbow for RH=No; Enclosure for LH=Yes; Enclosure for RH=No; HWC Conn=0"; HWC Depth "Z"=12 1/4"; HWC for LH=Yes; HWC for RH=No; Height=20"; Induction Width "C"=21"; Induction for LH=Yes; Induction for RH=No; Inlet for LH=Yes; Inlet for RH=No; Length=48"; Q5A=20"; Q5B=24"; Q5Q=20"; Radius=4 15/16"; Width=48"
- ESTW 3/4-hp - 10R 1ROW COIL W/O S/ELBOW: Connector Bottom LH=No; Connector Bottom RH=Yes; Connector Top LH=No; Connector Top RH=Yes; Diameter=9 7/8"; Discharge Width "X"=24"; Duct Inlet Radius=5"; Elbow for LH=No; Elbow for RH=No; Enclosure for LH=No; Enclosure for RH=Yes; HWC Conn=0"; HWC Depth "Z"=12 1/4"; HWC for LH=No; HWC for RH=Yes; Height=20"; Induction Width "C"=21"; Induction for LH=No; Induction for RH=Yes; Inlet for LH=No; Inlet for RH=Yes; Length=48"; Q5A=20"; Q5B=24"; Q5Q=20"; Radius=4 15/16"; Width=48"
- ESTW 3/4-hp - 10L 1ROW COIL WITH S/ELBOW: Connector Bottom LH=Yes; Connector Bottom RH=No; Connector Top LH=Yes; Connector Top RH=No; Diameter=9 7/8"; Discharge Width "X"=24"; Duct Inlet Radius=5"; Elbow for LH=Yes; Elbow for RH=No; Enclosure for LH=Yes; Enclosure for RH=No; HWC Conn=0"; HWC Depth "Z"=12 1/4"; HWC for LH=Yes; HWC for RH=No; Height=20"; Induction Width "C"=21"; Induction for LH=Yes; Induction for RH=No; Inlet for LH=Yes; Inlet for RH=No; Length=48"; Q5A=20"; Q5B=24"; Q5Q=20"; Radius=4 15/16"; Width=48"
- ESTW 3/4-hp - 10R 1ROW COIL WITH S/ELBOW: Connector Bottom LH=No; Connector Bottom RH=Yes; Connector Top LH=No; Connector Top RH=Yes; Diameter=9 7/8"; Discharge Width "X"=24"; Duct Inlet Radius=5"; Elbow for LH=No; Elbow for RH=Yes; Enclosure for LH=No; Enclosure for RH=Yes; HWC Conn=0"; HWC Depth "Z"=12 1/4"; HWC for LH=No; HWC for RH=Yes; Height=20"; Induction Width "C"=21"; Induction for LH=No; Induction for RH=Yes; Inlet for LH=No; Inlet for RH=Yes; Length=48"; Q5A=20"; Q5B=24"; Q5Q=20"; Radius=4 15/16"; Width=48"
- ESTW 3/4-hp - 10L 2ROW COIL W/O S/ELBOW: Connector Bottom LH=Yes; Connector Bottom RH=No; Connector Top LH=Yes; Connector Top RH=No; Diameter=9 7/8"; Discharge Width "X"=24"; Duct Inlet Radius=5"; Elbow for LH=No; Elbow for RH=No; Enclosure for LH=Yes; Enclosure for RH=No; HWC Conn=0"; HWC Depth "Z"=13 1/2"; HWC for LH=Yes; HWC for RH=No; Height=20"; Induction Width "C"=21"; Induction for LH=Yes; Induction for RH=No; Inlet for LH=Yes; Inlet for RH=No; Length=48"; Q5A=20"; Q5B=24"; Q5Q=20"; Radius=4 15/16"; Width=48"
- ESTW 3/4-hp - 10R 2ROW COIL W/O S/ELBOW: Connector Bottom LH=No; Connector Bottom RH=Yes; Connector Top LH=No; Connector Top RH=Yes; Diameter=9 7/8"; Discharge Width "X"=24"; Duct Inlet Radius=5"; Elbow for LH=No; Elbow for RH=No; Enclosure for LH=No; Enclosure for RH=Yes; HWC Conn=0"; HWC Depth "Z"=13 1/2"; HWC for LH=No; HWC for RH=Yes; Height=20"; Induction Width "C"=21"; Induction for LH=No; Induction for RH=Yes; Inlet for LH=No; Inlet for RH=Yes; Length=48"; Q5A=20"; Q5B=24"; Q5Q=20"; Radius=4 15/16"; Width=48"
- ESTW 3/4-hp - 10R 2ROW COIL WITH S/ELBOW: Connector Bottom LH=No; Connector Bottom RH=Yes; Connector Top LH=No; Connector Top RH=Yes; Diameter=9 7/8"; Discharge Width "X"=24"; Duct Inlet Radius=5"; Elbow for LH=No; Elbow for RH=Yes; Enclosure for LH=No; Enclosure for RH=Yes; HWC Conn=0"; HWC Depth "Z"=13 1/2"; HWC for LH=No; HWC for RH=Yes; Height=20"; Induction Width "C"=21"; Induction for LH=No; Induction for RH=Yes; Inlet for LH=No; Inlet for RH=Yes; Length=48"; Q5A=20"; Q5B=24"; Q5Q=20"; Radius=4 15/16"; Width=48"
- ESTW 3/4-hp - 10L 2ROW COIL WITH S/ELBOW: Connector Bottom LH=Yes; Connector Bottom RH=No; Connector Top LH=Yes; Connector Top RH=No; Diameter=9 7/8"; Discharge Width "X"=24"; Duct Inlet Radius=5"; Elbow for LH=Yes; Elbow for RH=No; Enclosure for LH=Yes; Enclosure for RH=No; HWC Conn=0"; HWC Depth "Z"=13 1/2"; HWC for LH=Yes; HWC for RH=No; Height=20"; Induction Width "C"=21"; Induction for LH=Yes; Induction for RH=No; Inlet for LH=Yes; Inlet for RH=No; Length=48"; Q5A=20"; Q5B=24"; Q5Q=20"; Radius=4 15/16"; Width=48"
- ESTW 3/4-hp - 12L 1ROW COIL W/O S/ELBOW: Connector Bottom LH=Yes; Connector Bottom RH=No; Connector Top LH=Yes; Connector Top RH=No; Diameter=11 7/8"; Discharge Width "X"=24"; Duct Inlet Radius=6"; Elbow for LH=No; Elbow for RH=No; Enclosure for LH=Yes; Enclosure for RH=No; HWC Conn=0"; HWC Depth "Z"=12 1/4"; HWC for LH=Yes; HWC for RH=No; Height=20"; Induction Width "C"=21"; Induction for LH=Yes; Induction for RH=No; Inlet for LH=Yes; Inlet for RH=No; Length=48"; Q5A=20"; Q5B=24"; Q5Q=20"; Radius=5 15/16"; Width=48"
- ESTW 3/4-hp - 12R 1ROW COIL W/O S/ELBOW: Connector Bottom LH=No; Connector Bottom RH=Yes; Connector Top LH=No; Connector Top RH=Yes; Diameter=11 7/8"; Discharge Width "X"=24"; Duct Inlet Radius=6"; Elbow for LH=No; Elbow for RH=No; Enclosure for LH=No; Enclosure for RH=Yes; HWC Conn=0"; HWC Depth "Z"=12 1/4"; HWC for LH=No; HWC for RH=Yes; Height=20"; Induction Width "C"=21"; Induction for LH=No; Induction for RH=Yes; Inlet for LH=No; Inlet for RH=Yes; Length=48"; Q5A=20"; Q5B=24"; Q5Q=20"; Radius=5 15/16"; Width=48"
- ESTW 3/4-hp - 12R 1ROW COIL WITH S/ELBOW: Connector Bottom LH=No; Connector Bottom RH=Yes; Connector Top LH=No; Connector Top RH=Yes; Diameter=11 7/8"; Discharge Width "X"=24"; Duct Inlet Radius=6"; Elbow for LH=No; Elbow for RH=Yes; Enclosure for LH=No; Enclosure for RH=Yes; HWC Conn=0"; HWC Depth "Z"=12 1/4"; HWC for LH=No; HWC for RH=Yes; Height=20"; Induction Width "C"=21"; Induction for LH=No; Induction for RH=Yes; Inlet for LH=No; Inlet for RH=Yes; Length=48"; Q5A=20"; Q5B=24"; Q5Q=20"; Radius=5 15/16"; Width=48"
- ESTW 3/4-hp - 12L 1ROW COIL WITH S/ELBOW: Connector Bottom LH=Yes; Connector Bottom RH=No; Connector Top LH=Yes; Connector Top RH=No; Diameter=11 7/8"; Discharge Width "X"=24"; Duct Inlet Radius=6"; Elbow for LH=Yes; Elbow for RH=No; Enclosure for LH=Yes; Enclosure for RH=No; HWC Conn=0"; HWC Depth "Z"=12 1/4"; HWC for LH=Yes; HWC for RH=No; Height=20"; Induction Width "C"=21"; Induction for LH=Yes; Induction for RH=No; Inlet for LH=Yes; Inlet for RH=No; Length=48"; Q5A=20"; Q5B=24"; Q5Q=20"; Radius=5 15/16"; Width=48"
- ESTW 3/4-hp - 12L 2ROW COIL W/O S/ELBOW: Connector Bottom LH=Yes; Connector Bottom RH=No; Connector Top LH=Yes; Connector Top RH=No; Diameter=11 7/8"; Discharge Width "X"=24"; Duct Inlet Radius=6"; Elbow for LH=No; Elbow for RH=No; Enclosure for LH=Yes; Enclosure for RH=No; HWC Conn=0"; HWC Depth "Z"=13 1/2"; HWC for LH=Yes; HWC for RH=No; Height=20"; Induction Width "C"=21"; Induction for LH=Yes; Induction for RH=No; Inlet for LH=Yes; Inlet for RH=No; Length=48"; Q5A=20"; Q5B=24"; Q5Q=20"; Radius=5 15/16"; Width=48"
- ESTW 3/4-hp - 12R 2ROW COIL W/O S/ELBOW: Connector Bottom LH=No; Connector Bottom RH=Yes; Connector Top LH=No; Connector Top RH=Yes; Diameter=11 7/8"; Discharge Width "X"=24"; Duct Inlet Radius=6"; Elbow for LH=No; Elbow for RH=No; Enclosure for LH=No; Enclosure for RH=Yes; HWC Conn=0"; HWC Depth "Z"=13 1/2"; HWC for LH=No; HWC for RH=Yes; Height=20"; Induction Width "C"=21"; Induction for LH=No; Induction for RH=Yes; Inlet for LH=No; Inlet for RH=Yes; Length=48"; Q5A=20"; Q5B=24"; Q5Q=20"; Radius=5 15/16"; Width=48"
- ESTW 3/4-hp - 12R 2ROW COIL WITH S/ELBOW: Connector Bottom LH=No; Connector Bottom RH=Yes; Connector Top LH=No; Connector Top RH=Yes; Diameter=11 7/8"; Discharge Width "X"=24"; Duct Inlet Radius=6"; Elbow for LH=No; Elbow for RH=Yes; Enclosure for LH=No; Enclosure for RH=Yes; HWC Conn=0"; HWC Depth "Z"=13 1/2"; HWC for LH=No; HWC for RH=Yes; Height=20"; Induction Width "C"=21"; Induction for LH=No; Induction for RH=Yes; Inlet for LH=No; Inlet for RH=Yes; Length=48"; Q5A=20"; Q5B=24"; Q5Q=20"; Radius=5 15/16"; Width=48"
- ESTW 3/4-hp - 12L 2ROW COIL WITH S/ELBOW: Connector Bottom LH=Yes; Connector Bottom RH=No; Connector Top LH=Yes; Connector Top RH=No; Diameter=11 7/8"; Discharge Width "X"=24"; Duct Inlet Radius=6"; Elbow for LH=No; Elbow for RH=No; Enclosure for LH=Yes; Enclosure for RH=No; HWC Conn=0"; HWC Depth "Z"=13 1/2"; HWC for LH=Yes; HWC for RH=No; Height=20"; Induction Width "C"=21"; Induction for LH=Yes; Induction for RH=No; Inlet for LH=Yes; Inlet for RH=No; Length=48"; Q5A=20"; Q5B=24"; Q5Q=20"; Radius=5 15/16"; Width=48"
- ESTW 3/4-hp - 14L 1ROW COIL W/O S/ELBOW: Connector Bottom LH=Yes; Connector Bottom RH=No; Connector Top LH=Yes; Connector Top RH=No; Diameter=13 7/8"; Discharge Width "X"=24"; Duct Inlet Radius=7"; Elbow for LH=No; Elbow for RH=No; Enclosure for LH=Yes; Enclosure for RH=No; HWC Conn=0"; HWC Depth "Z"=12 1/4"; HWC for LH=Yes; HWC for RH=No; Height=20"; Induction Width "C"=21"; Induction for LH=Yes; Induction for RH=No; Inlet for LH=Yes; Inlet for RH=No; Length=48"; Q5A=20"; Q5B=24"; Q5Q=20"; Radius=6 15/16"; Width=48"
- ESTW 3/4-hp - 14R 1ROW COIL W/O S/ELBOW: Connector Bottom LH=No; Connector Bottom RH=Yes; Connector Top LH=No; Connector Top RH=Yes; Diameter=13 7/8"; Discharge Width "X"=24"; Duct Inlet Radius=7"; Elbow for LH=No; Elbow for RH=No; Enclosure for LH=No; Enclosure for RH=Yes; HWC Conn=0"; HWC Depth "Z"=12 1/4"; HWC for LH=No; HWC for RH=Yes; Height=20"; Induction Width "C"=21"; Induction for LH=No; Induction for RH=Yes; Inlet for LH=No; Inlet for RH=Yes; Length=48"; Q5A=20"; Q5B=24"; Q5Q=20"; Radius=6 15/16"; Width=48"
- ESTW 3/4-hp - 14R 1ROW COIL WITH S/ELBOW: Connector Bottom LH=No; Connector Bottom RH=Yes; Connector Top LH=No; Connector Top RH=Yes; Diameter=13 7/8"; Discharge Width "X"=24"; Duct Inlet Radius=7"; Elbow for LH=No; Elbow for RH=Yes; Enclosure for LH=No; Enclosure for RH=Yes; HWC Conn=0"; HWC Depth "Z"=12 1/4"; HWC for LH=No; HWC for RH=Yes; Height=20"; Induction Width "C"=21"; Induction for LH=No; Induction for RH=Yes; Inlet for LH=No; Inlet for RH=Yes; Length=48"; Q5A=20"; Q5B=24"; Q5Q=20"; Radius=6 15/16"; Width=48"
- ESTW 3/4-hp - 14L 1ROW COIL WITH S/ELBOW: Connector Bottom LH=Yes; Connector Bottom RH=No; Connector Top LH=Yes; Connector Top RH=No; Diameter=13 7/8"; Discharge Width "X"=24"; Duct Inlet Radius=7"; Elbow for LH=Yes; Elbow for RH=No; Enclosure for LH=Yes; Enclosure for RH=No; HWC Conn=0"; HWC Depth "Z"=12 1/4"; HWC for LH=Yes; HWC for RH=No; Height=20"; Induction Width "C"=21"; Induction for LH=Yes; Induction for RH=No; Inlet for LH=Yes; Inlet for RH=No; Length=48"; Q5A=20"; Q5B=24"; Q5Q=20"; Radius=6 15/16"; Width=48"
- ESTW 3/4-hp - 14L 2ROW COIL W/O S/ELBOW: Connector Bottom LH=Yes; Connector Bottom RH=No; Connector Top LH=Yes; Connector Top RH=No; Diameter=13 7/8"; Discharge Width "X"=24"; Duct Inlet Radius=7"; Elbow for LH=No; Elbow for RH=No; Enclosure for LH=Yes; Enclosure for RH=No; HWC Conn=0"; HWC Depth "Z"=13 1/2"; HWC for LH=Yes; HWC for RH=No; Height=20"; Induction Width "C"=21"; Induction for LH=Yes; Induction for RH=No; Inlet for LH=Yes; Inlet for RH=No; Length=48"; Q5A=20"; Q5B=24"; Q5Q=20"; Radius=6 15/16"; Width=48"
- ESTW 3/4-hp - 14R 2ROW COIL W/O S/ELBOW: Connector Bottom LH=No; Connector Bottom RH=Yes; Connector Top LH=No; Connector Top RH=Yes; Diameter=13 7/8"; Discharge Width "X"=24"; Duct Inlet Radius=7"; Elbow for LH=No; Elbow for RH=No; Enclosure for LH=No; Enclosure for RH=Yes; HWC Conn=0"; HWC Depth "Z"=13 1/2"; HWC for LH=No; HWC for RH=Yes; Height=20"; Induction Width "C"=21"; Induction for LH=No; Induction for RH=Yes; Inlet for LH=No; Inlet for RH=Yes; Length=48"; Q5A=20"; Q5B=24"; Q5Q=20"; Radius=6 15/16"; Width=48"
- ESTW 3/4-hp - 14R 2ROW COIL WITH S/ELBOW: Connector Bottom LH=No; Connector Bottom RH=Yes; Connector Top LH=No; Connector Top RH=Yes; Diameter=13 7/8"; Discharge Width "X"=24"; Duct Inlet Radius=7"; Elbow for LH=No; Elbow for RH=Yes; Enclosure for LH=No; Enclosure for RH=Yes; HWC Conn=0"; HWC Depth "Z"=13 1/2"; HWC for LH=No; HWC for RH=Yes; Height=20"; Induction Width "C"=21"; Induction for LH=No; Induction for RH=Yes; Inlet for LH=No; Inlet for RH=Yes; Length=48"; Q5A=20"; Q5B=24"; Q5Q=20"; Radius=6 15/16"; Width=48"
- ESTW 3/4-hp - 14L 2ROW COIL WITH S/ELBOW: Connector Bottom LH=Yes; Connector Bottom RH=No; Connector Top LH=Yes; Connector Top RH=No; Diameter=13 7/8"; Discharge Width "X"=24"; Duct Inlet Radius=7"; Elbow for LH=Yes; Elbow for RH=No; Enclosure for LH=Yes; Enclosure for RH=No; HWC Conn=0"; HWC Depth "Z"=13 1/2"; HWC for LH=Yes; HWC for RH=No; Height=20"; Induction Width "C"=21"; Induction for LH=Yes; Induction for RH=No; Inlet for LH=Yes; Inlet for RH=No; Length=48"; Q5A=20"; Q5B=24"; Q5Q=20"; Radius=6 15/16"; Width=48"
- ESTW 3/4-hp - 16L 1ROW COIL W/O S/ELBOW: Connector Bottom LH=Yes; Connector Bottom RH=No; Connector Top LH=Yes; Connector Top RH=No; Diameter=15 7/8"; Discharge Width "X"=24"; Duct Inlet Radius=8"; Elbow for LH=No; Elbow for RH=No; Enclosure for LH=Yes; Enclosure for RH=No; HWC Conn=0"; HWC Depth "Z"=12 1/4"; HWC for LH=Yes; HWC for RH=No; Height=20"; Induction Width "C"=21"; Induction for LH=Yes; Induction for RH=No; Inlet for LH=Yes; Inlet for RH=No; Length=48"; Q5A=20"; Q5B=24"; Q5Q=20"; Radius=7 15/16"; Width=48"
- ESTW 3/4-hp - 16R 1ROW COIL W/O S/ELBOW: Connector Bottom LH=No; Connector Bottom RH=Yes; Connector Top LH=No; Connector Top RH=Yes; Diameter=15 7/8"; Discharge Width "X"=24"; Duct Inlet Radius=8"; Elbow for LH=No; Elbow for RH=No; Enclosure for LH=No; Enclosure for RH=Yes; HWC Conn=0"; HWC Depth "Z"=12 1/4"; HWC for LH=No; HWC for RH=Yes; Height=20"; Induction Width "C"=21"; Induction for LH=Yes; Induction for RH=Yes; Inlet for LH=No; Inlet for RH=Yes; Length=48"; Q5A=20"; Q5B=24"; Q5Q=20"; Radius=7 15/16"; Width=48"
- ESTW 3/4-hp - 16R 1ROW COIL WITH S/ELBOW: Connector Bottom LH=No; Connector Bottom RH=Yes; Connector Top LH=No; Connector Top RH=Yes; Diameter=15 7/8"; Discharge Width "X"=24"; Duct Inlet Radius=8"; Elbow for LH=No; Elbow for RH=Yes; Enclosure for LH=No; Enclosure for RH=Yes; HWC Conn=0"; HWC Depth "Z"=12 1/4"; HWC for LH=No; HWC for RH=Yes; Height=20"; Induction Width "C"=21"; Induction for LH=Yes; Induction for RH=Yes; Inlet for LH=No; Inlet for RH=Yes; Length=48"; Q5A=20"; Q5B=24"; Q5Q=20"; Radius=7 15/16"; Width=48"
- ESTW 3/4-hp - 16L 1ROW COIL WITH S/ELBOW: Connector Bottom LH=Yes; Connector Bottom RH=No; Connector Top LH=Yes; Connector Top RH=No; Diameter=15 7/8"; Discharge Width "X"=24"; Duct Inlet Radius=8"; Elbow for LH=Yes; Elbow for RH=No; Enclosure for LH=Yes; Enclosure for RH=No; HWC Conn=0"; HWC Depth "Z"=12 1/4"; HWC for LH=Yes; HWC for RH=No; Height=20"; Induction Width "C"=21"; Induction for LH=Yes; Induction for RH=No; Inlet for LH=Yes; Inlet for RH=No; Length=48"; Q5A=20"; Q5B=24"; Q5Q=20"; Radius=7 15/16"; Width=48"
- ESTW 3/4-hp - 16L 2ROW COIL W/O S/ELBOW: Connector Bottom LH=Yes; Connector Bottom RH=No; Connector Top LH=Yes; Connector Top RH=No; Diameter=15 7/8"; Discharge Width "X"=24"; Duct Inlet Radius=8"; Elbow for LH=No; Elbow for RH=No; Enclosure for LH=Yes; Enclosure for RH=No; HWC Conn=0"; HWC Depth "Z"=13 1/2"; HWC for LH=Yes; HWC for RH=No; Height=20"; Induction Width "C"=21"; Induction for LH=Yes; Induction for RH=No; Inlet for LH=Yes; Inlet for RH=No; Length=48"; Q5A=20"; Q5B=24"; Q5Q=20"; Radius=7 15/16"; Width=48"
- ESTW 3/4-hp - 16R 2ROW COIL W/O S/ELBOW: Connector Bottom LH=No; Connector Bottom RH=Yes; Connector Top LH=No; Connector Top RH=Yes; Diameter=15 7/8"; Discharge Width "X"=24"; Duct Inlet Radius=8"; Elbow for LH=No; Elbow for RH=No; Enclosure for LH=No; Enclosure for RH=Yes; HWC Conn=0"; HWC Depth "Z"=13 1/2"; HWC for LH=No; HWC for RH=Yes; Height=20"; Induction Width "C"=21"; Induction for LH=No; Induction for RH=Yes; Inlet for LH=No; Inlet for RH=Yes; Length=48"; Q5A=20"; Q5B=24"; Q5Q=20"; Radius=7 15/16"; Width=48"
- ESTW 3/4-hp - 16R 2ROW COIL WITH S/ELBOW: Connector Bottom LH=No; Connector Bottom RH=Yes; Connector Top LH=No; Connector Top RH=Yes; Diameter=15 7/8"; Discharge Width "X"=24"; Duct Inlet Radius=8"; Elbow for LH=No; Elbow for RH=Yes; Enclosure for LH=No; Enclosure for RH=Yes; HWC Conn=0"; HWC Depth "Z"=13 1/2"; HWC for LH=No; HWC for RH=Yes; Height=20"; Induction Width "C"=21"; Induction for LH=No; Induction for RH=Yes; Inlet for LH=No; Inlet for RH=Yes; Length=48"; Q5A=20"; Q5B=24"; Q5Q=20"; Radius=7 15/16"; Width=48"
- ESTW 3/4-hp - 16L 2ROW COIL WITH S/ELBOW: Connector Bottom LH=Yes; Connector Bottom RH=No; Connector Top LH=Yes; Connector Top RH=No; Diameter=15 7/8"; Discharge Width "X"=24"; Duct Inlet Radius=8"; Elbow for LH=Yes; Elbow for RH=No; Enclosure for LH=Yes; Enclosure for RH=No; HWC Conn=0"; HWC Depth "Z"=13 1/2"; HWC for LH=Yes; HWC for RH=No; Height=20"; Induction Width "C"=21"; Induction for LH=Yes; Induction for RH=No; Inlet for LH=Yes; Inlet for RH=No; Length=48"; Q5A=20"; Q5B=24"; Q5Q=20"; Radius=7 15/16"; Width=48"
- ESTW 1/3-hp - 07L 1ROW COIL W/O S/ELBOW: Connector Bottom LH=Yes; Connector Bottom RH=No; Connector Top LH=Yes; Connector Top RH=No; Diameter=6 7/8"; Discharge Width "X"=20"; Duct Inlet Radius=3"; Elbow for LH=No; Elbow for RH=No; Enclosure for LH=Yes; Enclosure for RH=No; HWC Conn=1"; HWC Depth "Z"=12 1/4"; HWC for LH=Yes; HWC for RH=No; Height=18"; Induction Width "C"=12"; Induction for LH=Yes; Induction for RH=No; Inlet for LH=Yes; Inlet for RH=No; Length=36"; Q5A=18"; Q5B=18"; Q5Q=18"; Radius=3 7/16"; Width=32"
- ESTW 1/3-hp - 07R 1ROW COIL W/O S/ELBOW: Connector Bottom LH=No; Connector Bottom RH=Yes; Connector Top LH=No; Connector Top RH=Yes; Diameter=6 7/8"; Discharge Width "X"=20"; Duct Inlet Radius=3"; Elbow for LH=No; Elbow for RH=No; Enclosure for LH=No; Enclosure for RH=Yes; HWC Conn=1"; HWC Depth "Z"=12 1/4"; HWC for LH=No; HWC for RH=Yes; Height=18"; Induction Width "C"=12"; Induction for LH=No; Induction for RH=Yes; Inlet for LH=No; Inlet for RH=Yes; Length=36"; Q5A=18"; Q5B=18"; Q5Q=18"; Radius=3 7/16"; Width=32"
- ESTW 1/3-hp - 07R 1ROW COIL WITH S/ELBOW: Connector Bottom LH=No; Connector Bottom RH=Yes; Connector Top LH=No; Connector Top RH=Yes; Diameter=6 7/8"; Discharge Width "X"=20"; Duct Inlet Radius=3"; Elbow for LH=No; Elbow for RH=Yes; Enclosure for LH=No; Enclosure for RH=Yes; HWC Conn=1"; HWC Depth "Z"=12 1/4"; HWC for LH=No; HWC for RH=Yes; Height=18"; Induction Width "C"=12"; Induction for LH=No; Induction for RH=Yes; Inlet for LH=No; Inlet for RH=Yes; Length=36"; Q5A=18"; Q5B=18"; Q5Q=18"; Radius=3 7/16"; Width=32"
- ESTW 1/3-hp - 07L 1ROW COIL WITH S/ELBOW: Connector Bottom LH=Yes; Connector Bottom RH=No; Connector Top LH=Yes; Connector Top RH=No; Diameter=6 7/8"; Discharge Width "X"=20"; Duct Inlet Radius=3"; Elbow for LH=Yes; Elbow for RH=No; Enclosure for LH=Yes; Enclosure for RH=No; HWC Conn=1"; HWC Depth "Z"=12 1/4"; HWC for LH=Yes; HWC for RH=No; Height=18"; Induction Width "C"=12"; Induction for LH=Yes; Induction for RH=No; Inlet for LH=Yes; Inlet for RH=No; Length=36"; Q5A=18"; Q5B=18"; Q5Q=18"; Radius=3 7/16"; Width=32"
- ESTW 1/3-hp - 07L 2ROW COIL WITH S/ELBOW: Connector Bottom LH=Yes; Connector Bottom RH=No; Connector Top LH=Yes; Connector Top RH=No; Diameter=6 7/8"; Discharge Width "X"=20"; Duct Inlet Radius=3"; Elbow for LH=Yes; Elbow for RH=No; Enclosure for LH=Yes; Enclosure for RH=No; HWC Conn=1"; HWC Depth "Z"=13 1/2"; HWC for LH=Yes; HWC for RH=No; Height=18"; Induction Width "C"=12"; Induction for LH=Yes; Induction for RH=No; Inlet for LH=Yes; Inlet for RH=No; Length=36"; Q5A=18"; Q5B=18"; Q5Q=18"; Radius=3 7/16"; Width=32"
- ESTW 1/3-hp - 07R 2ROW COIL WITH S/ELBOW: Connector Bottom LH=No; Connector Bottom RH=Yes; Connector Top LH=No; Connector Top RH=Yes; Diameter=6 7/8"; Discharge Width "X"=20"; Duct Inlet Radius=3"; Elbow for LH=No; Elbow for RH=Yes; Enclosure for LH=No; Enclosure for RH=Yes; HWC Conn=1"; HWC Depth "Z"=13 1/2"; HWC for LH=No; HWC for RH=Yes; Height=18"; Induction Width "C"=12"; Induction for LH=No; Induction for RH=Yes; Inlet for LH=No; Inlet for RH=Yes; Length=36"; Q5A=18"; Q5B=18"; Q5Q=18"; Radius=3 7/16"; Width=32"
- ESTW 1/3-hp - 07R 2ROW COIL W/O S/ELBOW: Connector Bottom LH=No; Connector Bottom RH=Yes; Connector Top LH=No; Connector Top RH=Yes; Diameter=6 7/8"; Discharge Width "X"=20"; Duct Inlet Radius=3"; Elbow for LH=No; Elbow for RH=No; Enclosure for LH=No; Enclosure for RH=Yes; HWC Conn=1"; HWC Depth "Z"=13 1/2"; HWC for LH=No; HWC for RH=Yes; Height=18"; Induction Width "C"=12"; Induction for LH=No; Induction for RH=Yes; Inlet for LH=No; Inlet for RH=Yes; Length=36"; Q5A=18"; Q5B=18"; Q5Q=18"; Radius=3 7/16"; Width=32"
- ESTW 1/3-hp - 07L 2ROW COIL W/O S/ELBOW: Connector Bottom LH=Yes; Connector Bottom RH=No; Connector Top LH=Yes; Connector Top RH=No; Diameter=6 7/8"; Discharge Width "X"=20"; Duct Inlet Radius=3"; Elbow for LH=No; Elbow for RH=No; Enclosure for LH=Yes; Enclosure for RH=No; HWC Conn=1"; HWC Depth "Z"=13 1/2"; HWC for LH=Yes; HWC for RH=No; Height=18"; Induction Width "C"=12"; Induction for LH=Yes; Induction for RH=No; Inlet for LH=Yes; Inlet for RH=No; Length=36"; Q5A=18"; Q5B=18"; Q5Q=18"; Radius=3 7/16"; Width=32"
- ESTW 1/3-hp - 06L 1ROW COIL W/O S/ELBOW: Connector Bottom LH=Yes; Connector Bottom RH=No; Connector Top LH=Yes; Connector Top RH=No; Diameter=5 7/8"; Discharge Width "X"=20"; Duct Inlet Radius=3"; Elbow for LH=No; Elbow for RH=No; Enclosure for LH=Yes; Enclosure for RH=No; HWC Conn=1"; HWC Depth "Z"=12 1/4"; HWC for LH=Yes; HWC for RH=No; Height=18"; Induction Width "C"=12"; Induction for LH=Yes; Induction for RH=No; Inlet for LH=Yes; Inlet for RH=No; Length=36"; Q5A=18"; Q5B=18"; Q5Q=18"; Radius=2 15/16"; Width=32"
- ESTW 1/3-hp - 06R 1ROW COIL W/O S/ELBOW: Connector Bottom LH=No; Connector Bottom RH=Yes; Connector Top LH=No; Connector Top RH=Yes; Diameter=5 7/8"; Discharge Width "X"=20"; Duct Inlet Radius=3"; Elbow for LH=No; Elbow for RH=No; Enclosure for LH=No; Enclosure for RH=Yes; HWC Conn=1"; HWC Depth "Z"=12 1/4"; HWC for LH=No; HWC for RH=Yes; Height=18"; Induction Width "C"=12"; Induction for LH=No; Induction for RH=Yes; Inlet for LH=No; Inlet for RH=Yes; Length=36"; Q5A=18"; Q5B=18"; Q5Q=18"; Radius=2 15/16"; Width=32"
- ESTW 1/3-hp - 06R 1ROW COIL WITH S/ELBOW: Connector Bottom LH=No; Connector Bottom RH=Yes; Connector Top LH=No; Connector Top RH=Yes; Diameter=5 7/8"; Discharge Width "X"=20"; Duct Inlet Radius=3"; Elbow for LH=No; Elbow for RH=Yes; Enclosure for LH=No; Enclosure for RH=Yes; HWC Conn=1"; HWC Depth "Z"=12 1/4"; HWC for LH=No; HWC for RH=Yes; Height=18"; Induction Width "C"=12"; Induction for LH=No; Induction for RH=Yes; Inlet for LH=No; Inlet for RH=Yes; Length=36"; Q5A=18"; Q5B=18"; Q5Q=18"; Radius=2 15/16"; Width=32"
- ESTW 1/3-hp - 06L 1ROW COIL WITH S/ELBOW: Connector Bottom LH=Yes; Connector Bottom RH=No; Connector Top LH=Yes; Connector Top RH=No; Diameter=5 7/8"; Discharge Width "X"=20"; Duct Inlet Radius=3"; Elbow for LH=Yes; Elbow for RH=No; Enclosure for LH=Yes; Enclosure for RH=No; HWC Conn=1"; HWC Depth "Z"=12 1/4"; HWC for LH=Yes; HWC for RH=No; Height=18"; Induction Width "C"=12"; Induction for LH=Yes; Induction for RH=No; Inlet for LH=Yes; Inlet for RH=No; Length=36"; Q5A=18"; Q5B=18"; Q5Q=18"; Radius=2 15/16"; Width=32"
- ESTW 1/3-hp - 06L 2ROW COIL W/O S/ELBOW: Connector Bottom LH=Yes; Connector Bottom RH=No; Connector Top LH=Yes; Connector Top RH=No; Diameter=5 7/8"; Discharge Width "X"=20"; Duct Inlet Radius=3"; Elbow for LH=No; Elbow for RH=No; Enclosure for LH=Yes; Enclosure for RH=No; HWC Conn=1"; HWC Depth "Z"=13 1/2"; HWC for LH=Yes; HWC for RH=No; Height=18"; Induction Width "C"=12"; Induction for LH=Yes; Induction for RH=No; Inlet for LH=Yes; Inlet for RH=No; Length=36"; Q5A=18"; Q5B=18"; Q5Q=18"; Radius=2 15/16"; Width=32"
- ESTW 1/3-hp - 06R 2ROW COIL W/O S/ELBOW: Connector Bottom LH=No; Connector Bottom RH=Yes; Connector Top LH=No; Connector Top RH=Yes; Diameter=5 7/8"; Discharge Width "X"=20"; Duct Inlet Radius=3"; Elbow for LH=No; Elbow for RH=No; Enclosure for LH=No; Enclosure for RH=Yes; HWC Conn=1"; HWC Depth "Z"=13 1/2"; HWC for LH=No; HWC for RH=Yes; Height=18"; Induction Width "C"=12"; Induction for LH=No; Induction for RH=Yes; Inlet for LH=No; Inlet for RH=Yes; Length=36"; Q5A=18"; Q5B=18"; Q5Q=18"; Radius=2 15/16"; Width=32"
- ESTW 1/3-hp - 06R 2ROW COIL WITH S/ELBOW: Connector Bottom LH=No; Connector Bottom RH=Yes; Connector Top LH=No; Connector Top RH=Yes; Diameter=5 7/8"; Discharge Width "X"=20"; Duct Inlet Radius=3"; Elbow for LH=No; Elbow for RH=Yes; Enclosure for LH=No; Enclosure for RH=Yes; HWC Conn=1"; HWC Depth "Z"=13 1/2"; HWC for LH=No; HWC for RH=Yes; Height=18"; Induction Width "C"=12"; Induction for LH=No; Induction for RH=Yes; Inlet for LH=No; Inlet for RH=Yes; Length=36"; Q5A=18"; Q5B=18"; Q5Q=18"; Radius=2 15/16"; Width=32"
- ESTW 1/3-hp - 06L 2ROW COIL WITH S/ELBOW: Connector Bottom LH=Yes; Connector Bottom RH=No; Connector Top LH=Yes; Connector Top RH=No; Diameter=5 7/8"; Discharge Width "X"=20"; Duct Inlet Radius=3"; Elbow for LH=Yes; Elbow for RH=No; Enclosure for LH=Yes; Enclosure for RH=No; HWC Conn=1"; HWC Depth "Z"=13 1/2"; HWC for LH=Yes; HWC for RH=No; Height=18"; Induction Width "C"=12"; Induction for LH=Yes; Induction for RH=No; Inlet for LH=Yes; Inlet for RH=No; Length=36"; Q5A=18"; Q5B=18"; Q5Q=18"; Radius=2 15/16"; Width=32"

## geometry (parser evidence)
native form markers: Sweep x3
no freeform markers — native parametric forms only
